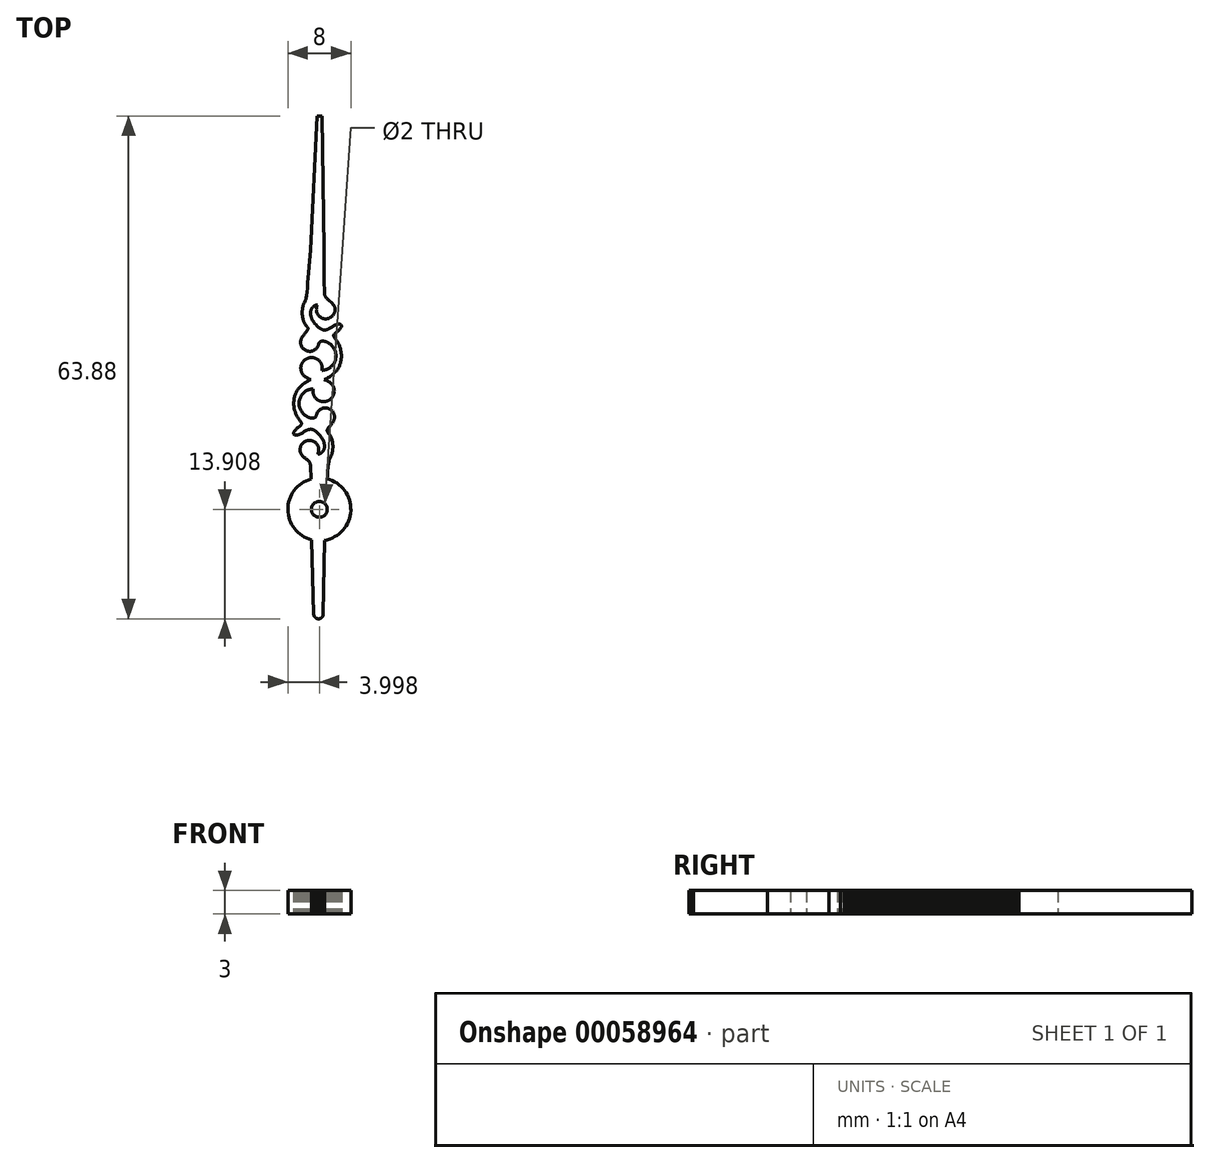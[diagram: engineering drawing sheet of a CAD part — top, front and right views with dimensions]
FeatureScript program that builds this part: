
annotation { "Feature Type Name" : "Feature", "Feature Type Description" : "" }
export const myFeature = defineFeature(function(context is Context, id is Id, definition is map)
    precondition{}
    {
        {
            var Q0;
            Q0=qCreatedBy(makeId("Top.planeOp"),FACE);
            var sketch = newSketch(context, id + "F0", { "sketchPlane" : qUnion([Q0])});
            skLineSegment(sketch, "E0", {"start": v(-0.08, 31.94) * mm, "end": v(0.58, 31.94) * mm});
            skLineSegment(sketch, "E1", {"start": v(0.58, 31.94) * mm, "end": v(0.8, 15.02) * mm});
            skLineSegment(sketch, "E2", {"start": v(0.8, 15.02) * mm, "end": v(0.8, 13.68) * mm});
            skLineSegment(sketch, "E3", {"start": v(0.8, 13.68) * mm, "end": v(0.82, 12.32) * mm});
            skLineSegment(sketch, "E4", {"start": v(0.82, 12.32) * mm, "end": v(0.83, 11.67) * mm});
            skLineSegment(sketch, "E5", {"start": v(0.83, 11.67) * mm, "end": v(0.84, 11.05) * mm});
            skLineSegment(sketch, "E6", {"start": v(0.84, 11.05) * mm, "end": v(0.85, 10.49) * mm});
            skLineSegment(sketch, "E7", {"start": v(0.85, 10.49) * mm, "end": v(0.87, 10) * mm});
            skLineSegment(sketch, "E8", {"start": v(0.87, 10) * mm, "end": v(0.89, 9.58) * mm});
            skLineSegment(sketch, "E9", {"start": v(0.89, 9.58) * mm, "end": v(0.9, 9.27) * mm});
            skLineSegment(sketch, "E10", {"start": v(0.9, 9.27) * mm, "end": v(0.92, 9.18) * mm});
            skLineSegment(sketch, "E11", {"start": v(0.92, 9.18) * mm, "end": v(0.94, 9.1) * mm});
            skLineSegment(sketch, "E12", {"start": v(0.94, 9.1) * mm, "end": v(0.97, 9.03) * mm});
            skLineSegment(sketch, "E13", {"start": v(0.97, 9.03) * mm, "end": v(1, 8.97) * mm});
            skLineSegment(sketch, "E14", {"start": v(1, 8.97) * mm, "end": v(1.03, 8.9) * mm});
            skLineSegment(sketch, "E15", {"start": v(1.03, 8.9) * mm, "end": v(1.07, 8.85) * mm});
            skLineSegment(sketch, "E16", {"start": v(1.07, 8.85) * mm, "end": v(1.12, 8.8) * mm});
            skLineSegment(sketch, "E17", {"start": v(1.12, 8.8) * mm, "end": v(1.16, 8.76) * mm});
            skLineSegment(sketch, "E18", {"start": v(1.16, 8.76) * mm, "end": v(1.26, 8.67) * mm});
            skLineSegment(sketch, "E19", {"start": v(1.26, 8.67) * mm, "end": v(1.36, 8.59) * mm});
            skLineSegment(sketch, "E20", {"start": v(1.36, 8.59) * mm, "end": v(1.45, 8.5) * mm});
            skLineSegment(sketch, "E21", {"start": v(1.45, 8.5) * mm, "end": v(1.5, 8.46) * mm});
            skLineSegment(sketch, "E22", {"start": v(1.5, 8.46) * mm, "end": v(1.54, 8.42) * mm});
            skLineSegment(sketch, "E23", {"start": v(1.54, 8.42) * mm, "end": v(1.54, 8.42) * mm});
            skLineSegment(sketch, "E24", {"start": v(1.54, 8.42) * mm, "end": v(1.69, 8.3) * mm});
            skLineSegment(sketch, "E25", {"start": v(1.69, 8.3) * mm, "end": v(1.76, 8.25) * mm});
            skLineSegment(sketch, "E26", {"start": v(1.76, 8.25) * mm, "end": v(1.82, 8.19) * mm});
            skLineSegment(sketch, "E27", {"start": v(1.82, 8.19) * mm, "end": v(1.88, 8.13) * mm});
            skLineSegment(sketch, "E28", {"start": v(1.88, 8.13) * mm, "end": v(1.94, 8.07) * mm});
            skLineSegment(sketch, "E29", {"start": v(1.94, 8.07) * mm, "end": v(2, 8) * mm});
            skLineSegment(sketch, "E30", {"start": v(2, 8) * mm, "end": v(2.04, 7.94) * mm});
            skLineSegment(sketch, "E31", {"start": v(2.04, 7.94) * mm, "end": v(2.08, 7.88) * mm});
            skLineSegment(sketch, "E32", {"start": v(2.08, 7.88) * mm, "end": v(2.12, 7.81) * mm});
            skLineSegment(sketch, "E33", {"start": v(2.12, 7.81) * mm, "end": v(2.15, 7.74) * mm});
            skLineSegment(sketch, "E34", {"start": v(2.15, 7.74) * mm, "end": v(2.17, 7.67) * mm});
            skLineSegment(sketch, "E35", {"start": v(2.17, 7.67) * mm, "end": v(2.2, 7.6) * mm});
            skLineSegment(sketch, "E36", {"start": v(2.2, 7.6) * mm, "end": v(2.2, 7.52) * mm});
            skLineSegment(sketch, "E37", {"start": v(2.2, 7.52) * mm, "end": v(2.22, 7.43) * mm});
            skLineSegment(sketch, "E38", {"start": v(2.22, 7.43) * mm, "end": v(2.22, 7.35) * mm});
            skLineSegment(sketch, "E39", {"start": v(2.22, 7.35) * mm, "end": v(2.22, 7.28) * mm});
            skLineSegment(sketch, "E40", {"start": v(2.22, 7.28) * mm, "end": v(2.21, 7.22) * mm});
            skLineSegment(sketch, "E41", {"start": v(2.21, 7.22) * mm, "end": v(2.2, 7.16) * mm});
            skLineSegment(sketch, "E42", {"start": v(2.2, 7.16) * mm, "end": v(2.2, 7.1) * mm});
            skLineSegment(sketch, "E43", {"start": v(2.2, 7.1) * mm, "end": v(2.18, 7.05) * mm});
            skLineSegment(sketch, "E44", {"start": v(2.18, 7.05) * mm, "end": v(2.17, 7) * mm});
            skLineSegment(sketch, "E45", {"start": v(2.17, 7) * mm, "end": v(2.15, 6.94) * mm});
            skLineSegment(sketch, "E46", {"start": v(2.15, 6.94) * mm, "end": v(2.13, 6.88) * mm});
            skLineSegment(sketch, "E47", {"start": v(2.13, 6.88) * mm, "end": v(2.1, 6.83) * mm});
            skLineSegment(sketch, "E48", {"start": v(2.1, 6.83) * mm, "end": v(2.08, 6.78) * mm});
            skLineSegment(sketch, "E49", {"start": v(2.08, 6.78) * mm, "end": v(2.02, 6.68) * mm});
            skLineSegment(sketch, "E50", {"start": v(2.02, 6.68) * mm, "end": v(1.95, 6.59) * mm});
            skLineSegment(sketch, "E51", {"start": v(1.95, 6.59) * mm, "end": v(1.87, 6.5) * mm});
            skLineSegment(sketch, "E52", {"start": v(1.87, 6.5) * mm, "end": v(1.79, 6.43) * mm});
            skLineSegment(sketch, "E53", {"start": v(1.79, 6.43) * mm, "end": v(1.7, 6.36) * mm});
            skLineSegment(sketch, "E54", {"start": v(1.7, 6.36) * mm, "end": v(1.6, 6.3) * mm});
            skLineSegment(sketch, "E55", {"start": v(1.6, 6.3) * mm, "end": v(1.55, 6.27) * mm});
            skLineSegment(sketch, "E56", {"start": v(1.55, 6.27) * mm, "end": v(1.5, 6.25) * mm});
            skLineSegment(sketch, "E57", {"start": v(1.5, 6.25) * mm, "end": v(1.44, 6.23) * mm});
            skLineSegment(sketch, "E58", {"start": v(1.44, 6.23) * mm, "end": v(1.39, 6.21) * mm});
            skLineSegment(sketch, "E59", {"start": v(1.39, 6.21) * mm, "end": v(1.33, 6.2) * mm});
            skLineSegment(sketch, "E60", {"start": v(1.33, 6.2) * mm, "end": v(1.27, 6.18) * mm});
            skLineSegment(sketch, "E61", {"start": v(1.27, 6.18) * mm, "end": v(1.21, 6.17) * mm});
            skLineSegment(sketch, "E62", {"start": v(1.21, 6.17) * mm, "end": v(1.15, 6.16) * mm});
            skLineSegment(sketch, "E63", {"start": v(1.15, 6.16) * mm, "end": v(1.1, 6.16) * mm});
            skLineSegment(sketch, "E64", {"start": v(1.1, 6.16) * mm, "end": v(1.03, 6.16) * mm});
            skLineSegment(sketch, "E65", {"start": v(1.03, 6.16) * mm, "end": v(0.97, 6.16) * mm});
            skLineSegment(sketch, "E66", {"start": v(0.97, 6.16) * mm, "end": v(0.91, 6.16) * mm});
            skLineSegment(sketch, "E67", {"start": v(0.91, 6.16) * mm, "end": v(0.85, 6.17) * mm});
            skLineSegment(sketch, "E68", {"start": v(0.85, 6.17) * mm, "end": v(0.8, 6.18) * mm});
            skLineSegment(sketch, "E69", {"start": v(0.8, 6.18) * mm, "end": v(0.74, 6.2) * mm});
            skLineSegment(sketch, "E70", {"start": v(0.74, 6.2) * mm, "end": v(0.68, 6.21) * mm});
            skLineSegment(sketch, "E71", {"start": v(0.68, 6.21) * mm, "end": v(0.62, 6.23) * mm});
            skLineSegment(sketch, "E72", {"start": v(0.62, 6.23) * mm, "end": v(0.57, 6.25) * mm});
            skLineSegment(sketch, "E73", {"start": v(0.57, 6.25) * mm, "end": v(0.52, 6.27) * mm});
            skLineSegment(sketch, "E74", {"start": v(0.52, 6.27) * mm, "end": v(0.47, 6.3) * mm});
            skLineSegment(sketch, "E75", {"start": v(0.47, 6.3) * mm, "end": v(0.37, 6.36) * mm});
            skLineSegment(sketch, "E76", {"start": v(0.37, 6.36) * mm, "end": v(0.28, 6.43) * mm});
            skLineSegment(sketch, "E77", {"start": v(0.28, 6.43) * mm, "end": v(0.2, 6.5) * mm});
            skLineSegment(sketch, "E78", {"start": v(0.2, 6.5) * mm, "end": v(0.12, 6.59) * mm});
            skLineSegment(sketch, "E79", {"start": v(0.12, 6.59) * mm, "end": v(0.05, 6.68) * mm});
            skLineSegment(sketch, "E80", {"start": v(0.05, 6.68) * mm, "end": v(-0.01, 6.78) * mm});
            skLineSegment(sketch, "E81", {"start": v(-0.01, 6.78) * mm, "end": v(-0.04, 6.83) * mm});
            skLineSegment(sketch, "E82", {"start": v(-0.04, 6.83) * mm, "end": v(-0.06, 6.88) * mm});
            skLineSegment(sketch, "E83", {"start": v(-0.06, 6.88) * mm, "end": v(-0.08, 6.94) * mm});
            skLineSegment(sketch, "E84", {"start": v(-0.08, 6.94) * mm, "end": v(-0.1, 7) * mm});
            skLineSegment(sketch, "E85", {"start": v(-0.1, 7) * mm, "end": v(-0.12, 7.05) * mm});
            skLineSegment(sketch, "E86", {"start": v(-0.12, 7.05) * mm, "end": v(-0.13, 7.1) * mm});
            skLineSegment(sketch, "E87", {"start": v(-0.13, 7.1) * mm, "end": v(-0.14, 7.16) * mm});
            skLineSegment(sketch, "E88", {"start": v(-0.14, 7.16) * mm, "end": v(-0.15, 7.22) * mm});
            skLineSegment(sketch, "E89", {"start": v(-0.15, 7.22) * mm, "end": v(-0.15, 7.28) * mm});
            skLineSegment(sketch, "E90", {"start": v(-0.15, 7.28) * mm, "end": v(-0.16, 7.35) * mm});
            skLineSegment(sketch, "E91", {"start": v(-0.16, 7.35) * mm, "end": v(-0.15, 7.42) * mm});
            skLineSegment(sketch, "E92", {"start": v(-0.15, 7.42) * mm, "end": v(-0.15, 7.5) * mm});
            skLineSegment(sketch, "E93", {"start": v(-0.15, 7.5) * mm, "end": v(-0.13, 7.58) * mm});
            skLineSegment(sketch, "E94", {"start": v(-0.13, 7.58) * mm, "end": v(-0.12, 7.65) * mm});
            skLineSegment(sketch, "E95", {"start": v(-0.12, 7.65) * mm, "end": v(-0.1, 7.73) * mm});
            skLineSegment(sketch, "E96", {"start": v(-0.1, 7.73) * mm, "end": v(-0.07, 7.8) * mm});
            skLineSegment(sketch, "E97", {"start": v(-0.07, 7.8) * mm, "end": v(-0.04, 7.87) * mm});
            skLineSegment(sketch, "E98", {"start": v(-0.04, 7.87) * mm, "end": v(0, 7.93) * mm});
            skLineSegment(sketch, "E99", {"start": v(0, 7.93) * mm, "end": v(-0.03, 7.93) * mm});
            skLineSegment(sketch, "E100", {"start": v(-0.03, 7.93) * mm, "end": v(-0.07, 7.92) * mm});
            skLineSegment(sketch, "E101", {"start": v(-0.07, 7.92) * mm, "end": v(-0.17, 7.88) * mm});
            skLineSegment(sketch, "E102", {"start": v(-0.17, 7.88) * mm, "end": v(-0.3, 7.83) * mm});
            skLineSegment(sketch, "E103", {"start": v(-0.3, 7.83) * mm, "end": v(-0.44, 7.76) * mm});
            skLineSegment(sketch, "E104", {"start": v(-0.44, 7.76) * mm, "end": v(-0.5, 7.72) * mm});
            skLineSegment(sketch, "E105", {"start": v(-0.5, 7.72) * mm, "end": v(-0.55, 7.69) * mm});
            skLineSegment(sketch, "E106", {"start": v(-0.55, 7.69) * mm, "end": v(-0.6, 7.65) * mm});
            skLineSegment(sketch, "E107", {"start": v(-0.6, 7.65) * mm, "end": v(-0.65, 7.6) * mm});
            skLineSegment(sketch, "E108", {"start": v(-0.65, 7.6) * mm, "end": v(-0.69, 7.56) * mm});
            skLineSegment(sketch, "E109", {"start": v(-0.69, 7.56) * mm, "end": v(-0.72, 7.5) * mm});
            skLineSegment(sketch, "E110", {"start": v(-0.72, 7.5) * mm, "end": v(-0.76, 7.45) * mm});
            skLineSegment(sketch, "E111", {"start": v(-0.76, 7.45) * mm, "end": v(-0.79, 7.4) * mm});
            skLineSegment(sketch, "E112", {"start": v(-0.79, 7.4) * mm, "end": v(-0.81, 7.34) * mm});
            skLineSegment(sketch, "E113", {"start": v(-0.81, 7.34) * mm, "end": v(-0.84, 7.27) * mm});
            skLineSegment(sketch, "E114", {"start": v(-0.84, 7.27) * mm, "end": v(-0.85, 7.2) * mm});
            skLineSegment(sketch, "E115", {"start": v(-0.85, 7.2) * mm, "end": v(-0.87, 7.14) * mm});
            skLineSegment(sketch, "E116", {"start": v(-0.87, 7.14) * mm, "end": v(-0.88, 7.07) * mm});
            skLineSegment(sketch, "E117", {"start": v(-0.88, 7.07) * mm, "end": v(-0.88, 7) * mm});
            skLineSegment(sketch, "E118", {"start": v(-0.88, 7) * mm, "end": v(-0.89, 6.93) * mm});
            skLineSegment(sketch, "E119", {"start": v(-0.89, 6.93) * mm, "end": v(-0.89, 6.86) * mm});
            skLineSegment(sketch, "E120", {"start": v(-0.89, 6.86) * mm, "end": v(-0.88, 6.78) * mm});
            skLineSegment(sketch, "E121", {"start": v(-0.88, 6.78) * mm, "end": v(-0.87, 6.7) * mm});
            skLineSegment(sketch, "E122", {"start": v(-0.87, 6.7) * mm, "end": v(-0.86, 6.62) * mm});
            skLineSegment(sketch, "E123", {"start": v(-0.86, 6.62) * mm, "end": v(-0.84, 6.55) * mm});
            skLineSegment(sketch, "E124", {"start": v(-0.84, 6.55) * mm, "end": v(-0.82, 6.46) * mm});
            skLineSegment(sketch, "E125", {"start": v(-0.82, 6.46) * mm, "end": v(-0.8, 6.38) * mm});
            skLineSegment(sketch, "E126", {"start": v(-0.8, 6.38) * mm, "end": v(-0.77, 6.3) * mm});
            skLineSegment(sketch, "E127", {"start": v(-0.77, 6.3) * mm, "end": v(-0.74, 6.22) * mm});
            skLineSegment(sketch, "E128", {"start": v(-0.74, 6.22) * mm, "end": v(-0.7, 6.14) * mm});
            skLineSegment(sketch, "E129", {"start": v(-0.7, 6.14) * mm, "end": v(-0.67, 6.06) * mm});
            skLineSegment(sketch, "E130", {"start": v(-0.67, 6.06) * mm, "end": v(-0.62, 5.98) * mm});
            skLineSegment(sketch, "E131", {"start": v(-0.62, 5.98) * mm, "end": v(-0.58, 5.9) * mm});
            skLineSegment(sketch, "E132", {"start": v(-0.58, 5.9) * mm, "end": v(-0.53, 5.82) * mm});
            skLineSegment(sketch, "E133", {"start": v(-0.53, 5.82) * mm, "end": v(-0.47, 5.74) * mm});
            skLineSegment(sketch, "E134", {"start": v(-0.47, 5.74) * mm, "end": v(-0.42, 5.66) * mm});
            skLineSegment(sketch, "E135", {"start": v(-0.42, 5.66) * mm, "end": v(-0.35, 5.58) * mm});
            skLineSegment(sketch, "E136", {"start": v(-0.35, 5.58) * mm, "end": v(-0.22, 5.41) * mm});
            skLineSegment(sketch, "E137", {"start": v(-0.22, 5.41) * mm, "end": v(-0.08, 5.27) * mm});
            skLineSegment(sketch, "E138", {"start": v(-0.08, 5.27) * mm, "end": v(0.05, 5.14) * mm});
            skLineSegment(sketch, "E139", {"start": v(0.05, 5.14) * mm, "end": v(0.11, 5.08) * mm});
            skLineSegment(sketch, "E140", {"start": v(0.11, 5.08) * mm, "end": v(0.18, 5.03) * mm});
            skLineSegment(sketch, "E141", {"start": v(0.18, 5.03) * mm, "end": v(0.24, 4.98) * mm});
            skLineSegment(sketch, "E142", {"start": v(0.24, 4.98) * mm, "end": v(0.3, 4.94) * mm});
            skLineSegment(sketch, "E143", {"start": v(0.3, 4.94) * mm, "end": v(0.36, 4.9) * mm});
            skLineSegment(sketch, "E144", {"start": v(0.36, 4.9) * mm, "end": v(0.42, 4.87) * mm});
            skLineSegment(sketch, "E145", {"start": v(0.42, 4.87) * mm, "end": v(0.48, 4.84) * mm});
            skLineSegment(sketch, "E146", {"start": v(0.48, 4.84) * mm, "end": v(0.54, 4.81) * mm});
            skLineSegment(sketch, "E147", {"start": v(0.54, 4.81) * mm, "end": v(0.6, 4.79) * mm});
            skLineSegment(sketch, "E148", {"start": v(0.6, 4.79) * mm, "end": v(0.66, 4.77) * mm});
            skLineSegment(sketch, "E149", {"start": v(0.66, 4.77) * mm, "end": v(0.72, 4.76) * mm});
            skLineSegment(sketch, "E150", {"start": v(0.72, 4.76) * mm, "end": v(0.78, 4.75) * mm});
            skLineSegment(sketch, "E151", {"start": v(0.78, 4.75) * mm, "end": v(0.85, 4.75) * mm});
            skLineSegment(sketch, "E152", {"start": v(0.85, 4.75) * mm, "end": v(0.9, 4.74) * mm});
            skLineSegment(sketch, "E153", {"start": v(0.9, 4.74) * mm, "end": v(0.97, 4.75) * mm});
            skLineSegment(sketch, "E154", {"start": v(0.97, 4.75) * mm, "end": v(1.03, 4.76) * mm});
            skLineSegment(sketch, "E155", {"start": v(1.03, 4.76) * mm, "end": v(1.1, 4.77) * mm});
            skLineSegment(sketch, "E156", {"start": v(1.1, 4.77) * mm, "end": v(1.16, 4.79) * mm});
            skLineSegment(sketch, "E157", {"start": v(1.16, 4.79) * mm, "end": v(1.22, 4.8) * mm});
            skLineSegment(sketch, "E158", {"start": v(1.22, 4.8) * mm, "end": v(1.29, 4.83) * mm});
            skLineSegment(sketch, "E159", {"start": v(1.29, 4.83) * mm, "end": v(1.35, 4.86) * mm});
            skLineSegment(sketch, "E160", {"start": v(1.35, 4.86) * mm, "end": v(1.42, 4.9) * mm});
            skLineSegment(sketch, "E161", {"start": v(1.42, 4.9) * mm, "end": v(1.49, 4.93) * mm});
            skLineSegment(sketch, "E162", {"start": v(1.49, 4.93) * mm, "end": v(1.56, 4.97) * mm});
            skLineSegment(sketch, "E163", {"start": v(1.56, 4.97) * mm, "end": v(1.7, 5.06) * mm});
            skLineSegment(sketch, "E164", {"start": v(1.7, 5.06) * mm, "end": v(1.81, 5.14) * mm});
            skLineSegment(sketch, "E165", {"start": v(1.81, 5.14) * mm, "end": v(1.92, 5.2) * mm});
            skLineSegment(sketch, "E166", {"start": v(1.92, 5.2) * mm, "end": v(2.03, 5.26) * mm});
            skLineSegment(sketch, "E167", {"start": v(2.03, 5.26) * mm, "end": v(2.13, 5.31) * mm});
            skLineSegment(sketch, "E168", {"start": v(2.13, 5.31) * mm, "end": v(2.22, 5.36) * mm});
            skLineSegment(sketch, "E169", {"start": v(2.22, 5.36) * mm, "end": v(2.32, 5.4) * mm});
            skLineSegment(sketch, "E170", {"start": v(2.32, 5.4) * mm, "end": v(2.4, 5.43) * mm});
            skLineSegment(sketch, "E171", {"start": v(2.4, 5.43) * mm, "end": v(2.49, 5.45) * mm});
            skLineSegment(sketch, "E172", {"start": v(2.49, 5.45) * mm, "end": v(2.57, 5.47) * mm});
            skLineSegment(sketch, "E173", {"start": v(2.57, 5.47) * mm, "end": v(2.64, 5.48) * mm});
            skLineSegment(sketch, "E174", {"start": v(2.64, 5.48) * mm, "end": v(2.71, 5.49) * mm});
            skLineSegment(sketch, "E175", {"start": v(2.71, 5.49) * mm, "end": v(2.77, 5.49) * mm});
            skLineSegment(sketch, "E176", {"start": v(2.77, 5.49) * mm, "end": v(2.83, 5.48) * mm});
            skLineSegment(sketch, "E177", {"start": v(2.83, 5.48) * mm, "end": v(2.88, 5.47) * mm});
            skLineSegment(sketch, "E178", {"start": v(2.88, 5.47) * mm, "end": v(2.93, 5.45) * mm});
            skLineSegment(sketch, "E179", {"start": v(2.93, 5.45) * mm, "end": v(2.96, 5.43) * mm});
            skLineSegment(sketch, "E180", {"start": v(2.96, 5.43) * mm, "end": v(3, 5.4) * mm});
            skLineSegment(sketch, "E181", {"start": v(3, 5.4) * mm, "end": v(3.02, 5.37) * mm});
            skLineSegment(sketch, "E182", {"start": v(3.02, 5.37) * mm, "end": v(3.04, 5.34) * mm});
            skLineSegment(sketch, "E183", {"start": v(3.04, 5.34) * mm, "end": v(3.05, 5.3) * mm});
            skLineSegment(sketch, "E184", {"start": v(3.05, 5.3) * mm, "end": v(3.05, 5.25) * mm});
            skLineSegment(sketch, "E185", {"start": v(3.05, 5.25) * mm, "end": v(3.04, 5.2) * mm});
            skLineSegment(sketch, "E186", {"start": v(3.04, 5.2) * mm, "end": v(3.03, 5.15) * mm});
            skLineSegment(sketch, "E187", {"start": v(3.03, 5.15) * mm, "end": v(3, 5.1) * mm});
            skLineSegment(sketch, "E188", {"start": v(3, 5.1) * mm, "end": v(2.97, 5.03) * mm});
            skLineSegment(sketch, "E189", {"start": v(2.97, 5.03) * mm, "end": v(2.93, 4.97) * mm});
            skLineSegment(sketch, "E190", {"start": v(2.93, 4.97) * mm, "end": v(2.88, 4.9) * mm});
            skLineSegment(sketch, "E191", {"start": v(2.88, 4.9) * mm, "end": v(2.82, 4.83) * mm});
            skLineSegment(sketch, "E192", {"start": v(2.82, 4.83) * mm, "end": v(2.75, 4.76) * mm});
            skLineSegment(sketch, "E193", {"start": v(2.75, 4.76) * mm, "end": v(2.67, 4.68) * mm});
            skLineSegment(sketch, "E194", {"start": v(2.67, 4.68) * mm, "end": v(2.58, 4.6) * mm});
            skLineSegment(sketch, "E195", {"start": v(2.58, 4.6) * mm, "end": v(2.48, 4.52) * mm});
            skLineSegment(sketch, "E196", {"start": v(2.48, 4.52) * mm, "end": v(2.3, 4.38) * mm});
            skLineSegment(sketch, "E197", {"start": v(2.3, 4.38) * mm, "end": v(2.22, 4.31) * mm});
            skLineSegment(sketch, "E198", {"start": v(2.22, 4.31) * mm, "end": v(2.16, 4.26) * mm});
            skLineSegment(sketch, "E199", {"start": v(2.16, 4.26) * mm, "end": v(2.11, 4.2) * mm});
            skLineSegment(sketch, "E200", {"start": v(2.11, 4.2) * mm, "end": v(2.08, 4.15) * mm});
            skLineSegment(sketch, "E201", {"start": v(2.08, 4.15) * mm, "end": v(2.06, 4.12) * mm});
            skLineSegment(sketch, "E202", {"start": v(2.06, 4.12) * mm, "end": v(2.06, 4.1) * mm});
            skLineSegment(sketch, "E203", {"start": v(2.06, 4.1) * mm, "end": v(2.05, 4.07) * mm});
            skLineSegment(sketch, "E204", {"start": v(2.05, 4.07) * mm, "end": v(2.05, 4.04) * mm});
            skLineSegment(sketch, "E205", {"start": v(2.05, 4.04) * mm, "end": v(2.05, 4.01) * mm});
            skLineSegment(sketch, "E206", {"start": v(2.05, 4.01) * mm, "end": v(2.05, 3.98) * mm});
            skLineSegment(sketch, "E207", {"start": v(2.05, 3.98) * mm, "end": v(2.07, 3.92) * mm});
            skLineSegment(sketch, "E208", {"start": v(2.07, 3.92) * mm, "end": v(2.1, 3.85) * mm});
            skLineSegment(sketch, "E209", {"start": v(2.1, 3.85) * mm, "end": v(2.15, 3.76) * mm});
            skLineSegment(sketch, "E210", {"start": v(2.15, 3.76) * mm, "end": v(2.2, 3.67) * mm});
            skLineSegment(sketch, "E211", {"start": v(2.2, 3.67) * mm, "end": v(2.28, 3.57) * mm});
            skLineSegment(sketch, "E212", {"start": v(2.28, 3.57) * mm, "end": v(2.46, 3.31) * mm});
            skLineSegment(sketch, "E213", {"start": v(2.46, 3.31) * mm, "end": v(2.53, 3.2) * mm});
            skLineSegment(sketch, "E214", {"start": v(2.53, 3.2) * mm, "end": v(2.6, 3.1) * mm});
            skLineSegment(sketch, "E215", {"start": v(2.6, 3.1) * mm, "end": v(2.66, 3) * mm});
            skLineSegment(sketch, "E216", {"start": v(2.66, 3) * mm, "end": v(2.71, 2.88) * mm});
            skLineSegment(sketch, "E217", {"start": v(2.71, 2.88) * mm, "end": v(2.77, 2.76) * mm});
            skLineSegment(sketch, "E218", {"start": v(2.77, 2.76) * mm, "end": v(2.81, 2.64) * mm});
            skLineSegment(sketch, "E219", {"start": v(2.81, 2.64) * mm, "end": v(2.86, 2.52) * mm});
            skLineSegment(sketch, "E220", {"start": v(2.86, 2.52) * mm, "end": v(2.9, 2.4) * mm});
            skLineSegment(sketch, "E221", {"start": v(2.9, 2.4) * mm, "end": v(2.93, 2.27) * mm});
            skLineSegment(sketch, "E222", {"start": v(2.93, 2.27) * mm, "end": v(2.96, 2.15) * mm});
            skLineSegment(sketch, "E223", {"start": v(2.96, 2.15) * mm, "end": v(2.98, 2.02) * mm});
            skLineSegment(sketch, "E224", {"start": v(2.98, 2.02) * mm, "end": v(3, 1.9) * mm});
            skLineSegment(sketch, "E225", {"start": v(3, 1.9) * mm, "end": v(3.01, 1.77) * mm});
            skLineSegment(sketch, "E226", {"start": v(3.01, 1.77) * mm, "end": v(3.02, 1.64) * mm});
            skLineSegment(sketch, "E227", {"start": v(3.02, 1.64) * mm, "end": v(3.03, 1.51) * mm});
            skLineSegment(sketch, "E228", {"start": v(3.03, 1.51) * mm, "end": v(3.03, 1.38) * mm});
            skLineSegment(sketch, "E229", {"start": v(3.03, 1.38) * mm, "end": v(3.02, 1.26) * mm});
            skLineSegment(sketch, "E230", {"start": v(3.02, 1.26) * mm, "end": v(3.01, 1.13) * mm});
            skLineSegment(sketch, "E231", {"start": v(3.01, 1.13) * mm, "end": v(3, 1) * mm});
            skLineSegment(sketch, "E232", {"start": v(3, 1) * mm, "end": v(2.98, 0.88) * mm});
            skLineSegment(sketch, "E233", {"start": v(2.98, 0.88) * mm, "end": v(2.95, 0.75) * mm});
            skLineSegment(sketch, "E234", {"start": v(2.95, 0.75) * mm, "end": v(2.93, 0.63) * mm});
            skLineSegment(sketch, "E235", {"start": v(2.93, 0.63) * mm, "end": v(2.9, 0.51) * mm});
            skLineSegment(sketch, "E236", {"start": v(2.9, 0.51) * mm, "end": v(2.86, 0.4) * mm});
            skLineSegment(sketch, "E237", {"start": v(2.86, 0.4) * mm, "end": v(2.81, 0.28) * mm});
            skLineSegment(sketch, "E238", {"start": v(2.81, 0.28) * mm, "end": v(2.77, 0.17) * mm});
            skLineSegment(sketch, "E239", {"start": v(2.77, 0.17) * mm, "end": v(2.71, 0.06) * mm});
            skLineSegment(sketch, "E240", {"start": v(2.71, 0.06) * mm, "end": v(2.66, -0.05) * mm});
            skLineSegment(sketch, "E241", {"start": v(2.66, -0.05) * mm, "end": v(2.6, -0.15) * mm});
            skLineSegment(sketch, "E242", {"start": v(2.6, -0.15) * mm, "end": v(2.53, -0.25) * mm});
            skLineSegment(sketch, "E243", {"start": v(2.53, -0.25) * mm, "end": v(2.46, -0.35) * mm});
            skLineSegment(sketch, "E244", {"start": v(2.46, -0.35) * mm, "end": v(2.39, -0.44) * mm});
            skLineSegment(sketch, "E245", {"start": v(2.39, -0.44) * mm, "end": v(2.25, -0.59) * mm});
            skLineSegment(sketch, "E246", {"start": v(2.25, -0.59) * mm, "end": v(2.1, -0.73) * mm});
            skLineSegment(sketch, "E247", {"start": v(2.1, -0.73) * mm, "end": v(1.96, -0.87) * mm});
            skLineSegment(sketch, "E248", {"start": v(1.96, -0.87) * mm, "end": v(1.81, -1) * mm});
            skLineSegment(sketch, "E249", {"start": v(1.81, -1) * mm, "end": v(1.66, -1.1) * mm});
            skLineSegment(sketch, "E250", {"start": v(1.66, -1.1) * mm, "end": v(1.5, -1.22) * mm});
            skLineSegment(sketch, "E251", {"start": v(1.5, -1.22) * mm, "end": v(1.35, -1.31) * mm});
            skLineSegment(sketch, "E252", {"start": v(1.35, -1.31) * mm, "end": v(1.2, -1.4) * mm});
            skLineSegment(sketch, "E253", {"start": v(1.2, -1.4) * mm, "end": v(1.03, -1.48) * mm});
            skLineSegment(sketch, "E254", {"start": v(1.03, -1.48) * mm, "end": v(0.87, -1.55) * mm});
            skLineSegment(sketch, "E255", {"start": v(0.87, -1.55) * mm, "end": v(0.85, -1.55) * mm});
            skLineSegment(sketch, "E256", {"start": v(0.85, -1.55) * mm, "end": v(0.94, -1.59) * mm});
            skLineSegment(sketch, "E257", {"start": v(0.94, -1.59) * mm, "end": v(1.06, -1.64) * mm});
            skLineSegment(sketch, "E258", {"start": v(1.06, -1.64) * mm, "end": v(1.26, -1.73) * mm});
            skLineSegment(sketch, "E259", {"start": v(1.26, -1.73) * mm, "end": v(1.4, -1.8) * mm});
            skLineSegment(sketch, "E260", {"start": v(1.4, -1.8) * mm, "end": v(1.47, -1.83) * mm});
            skLineSegment(sketch, "E261", {"start": v(1.47, -1.83) * mm, "end": v(1.54, -1.88) * mm});
            skLineSegment(sketch, "E262", {"start": v(1.54, -1.88) * mm, "end": v(1.6, -1.93) * mm});
            skLineSegment(sketch, "E263", {"start": v(1.6, -1.93) * mm, "end": v(1.67, -1.99) * mm});
            skLineSegment(sketch, "E264", {"start": v(1.67, -1.99) * mm, "end": v(1.74, -2.05) * mm});
            skLineSegment(sketch, "E265", {"start": v(1.74, -2.05) * mm, "end": v(1.8, -2.1) * mm});
            skLineSegment(sketch, "E266", {"start": v(1.8, -2.1) * mm, "end": v(1.85, -2.18) * mm});
            skLineSegment(sketch, "E267", {"start": v(1.85, -2.18) * mm, "end": v(1.9, -2.25) * mm});
            skLineSegment(sketch, "E268", {"start": v(1.9, -2.25) * mm, "end": v(1.95, -2.32) * mm});
            skLineSegment(sketch, "E269", {"start": v(1.95, -2.32) * mm, "end": v(1.99, -2.4) * mm});
            skLineSegment(sketch, "E270", {"start": v(1.99, -2.4) * mm, "end": v(2.02, -2.48) * mm});
            skLineSegment(sketch, "E271", {"start": v(2.02, -2.48) * mm, "end": v(2.06, -2.56) * mm});
            skLineSegment(sketch, "E272", {"start": v(2.06, -2.56) * mm, "end": v(2.08, -2.64) * mm});
            skLineSegment(sketch, "E273", {"start": v(2.08, -2.64) * mm, "end": v(2.1, -2.73) * mm});
            skLineSegment(sketch, "E274", {"start": v(2.1, -2.73) * mm, "end": v(2.12, -2.82) * mm});
            skLineSegment(sketch, "E275", {"start": v(2.12, -2.82) * mm, "end": v(2.13, -2.9) * mm});
            skLineSegment(sketch, "E276", {"start": v(2.13, -2.9) * mm, "end": v(2.13, -3) * mm});
            skLineSegment(sketch, "E277", {"start": v(2.13, -3) * mm, "end": v(2.13, -3.07) * mm});
            skLineSegment(sketch, "E278", {"start": v(2.13, -3.07) * mm, "end": v(2.12, -3.14) * mm});
            skLineSegment(sketch, "E279", {"start": v(2.12, -3.14) * mm, "end": v(2.11, -3.2) * mm});
            skLineSegment(sketch, "E280", {"start": v(2.11, -3.2) * mm, "end": v(2.1, -3.28) * mm});
            skLineSegment(sketch, "E281", {"start": v(2.1, -3.28) * mm, "end": v(2.09, -3.34) * mm});
            skLineSegment(sketch, "E282", {"start": v(2.09, -3.34) * mm, "end": v(2.07, -3.4) * mm});
            skLineSegment(sketch, "E283", {"start": v(2.07, -3.4) * mm, "end": v(2.05, -3.47) * mm});
            skLineSegment(sketch, "E284", {"start": v(2.05, -3.47) * mm, "end": v(2.02, -3.53) * mm});
            skLineSegment(sketch, "E285", {"start": v(2.02, -3.53) * mm, "end": v(2, -3.6) * mm});
            skLineSegment(sketch, "E286", {"start": v(2, -3.6) * mm, "end": v(1.96, -3.65) * mm});
            skLineSegment(sketch, "E287", {"start": v(1.96, -3.65) * mm, "end": v(1.93, -3.7) * mm});
            skLineSegment(sketch, "E288", {"start": v(1.93, -3.7) * mm, "end": v(1.9, -3.76) * mm});
            skLineSegment(sketch, "E289", {"start": v(1.9, -3.76) * mm, "end": v(1.86, -3.82) * mm});
            skLineSegment(sketch, "E290", {"start": v(1.86, -3.82) * mm, "end": v(1.82, -3.87) * mm});
            skLineSegment(sketch, "E291", {"start": v(1.82, -3.87) * mm, "end": v(1.77, -3.92) * mm});
            skLineSegment(sketch, "E292", {"start": v(1.77, -3.92) * mm, "end": v(1.73, -3.97) * mm});
            skLineSegment(sketch, "E293", {"start": v(1.73, -3.97) * mm, "end": v(1.68, -4.01) * mm});
            skLineSegment(sketch, "E294", {"start": v(1.68, -4.01) * mm, "end": v(1.63, -4.05) * mm});
            skLineSegment(sketch, "E295", {"start": v(1.63, -4.05) * mm, "end": v(1.58, -4.1) * mm});
            skLineSegment(sketch, "E296", {"start": v(1.58, -4.1) * mm, "end": v(1.53, -4.13) * mm});
            skLineSegment(sketch, "E297", {"start": v(1.53, -4.13) * mm, "end": v(1.47, -4.17) * mm});
            skLineSegment(sketch, "E298", {"start": v(1.47, -4.17) * mm, "end": v(1.42, -4.2) * mm});
            skLineSegment(sketch, "E299", {"start": v(1.42, -4.2) * mm, "end": v(1.36, -4.23) * mm});
            skLineSegment(sketch, "E300", {"start": v(1.36, -4.23) * mm, "end": v(1.3, -4.26) * mm});
            skLineSegment(sketch, "E301", {"start": v(1.3, -4.26) * mm, "end": v(1.23, -4.28) * mm});
            skLineSegment(sketch, "E302", {"start": v(1.23, -4.28) * mm, "end": v(1.17, -4.3) * mm});
            skLineSegment(sketch, "E303", {"start": v(1.17, -4.3) * mm, "end": v(1.1, -4.32) * mm});
            skLineSegment(sketch, "E304", {"start": v(1.1, -4.32) * mm, "end": v(1.04, -4.34) * mm});
            skLineSegment(sketch, "E305", {"start": v(1.04, -4.34) * mm, "end": v(0.97, -4.35) * mm});
            skLineSegment(sketch, "E306", {"start": v(0.97, -4.35) * mm, "end": v(0.9, -4.36) * mm});
            skLineSegment(sketch, "E307", {"start": v(0.9, -4.36) * mm, "end": v(0.84, -4.36) * mm});
            skLineSegment(sketch, "E308", {"start": v(0.84, -4.36) * mm, "end": v(0.76, -4.37) * mm});
            skLineSegment(sketch, "E309", {"start": v(0.76, -4.37) * mm, "end": v(0.7, -4.36) * mm});
            skLineSegment(sketch, "E310", {"start": v(0.7, -4.36) * mm, "end": v(0.63, -4.36) * mm});
            skLineSegment(sketch, "E311", {"start": v(0.63, -4.36) * mm, "end": v(0.56, -4.35) * mm});
            skLineSegment(sketch, "E312", {"start": v(0.56, -4.35) * mm, "end": v(0.5, -4.34) * mm});
            skLineSegment(sketch, "E313", {"start": v(0.5, -4.34) * mm, "end": v(0.42, -4.32) * mm});
            skLineSegment(sketch, "E314", {"start": v(0.42, -4.32) * mm, "end": v(0.36, -4.3) * mm});
            skLineSegment(sketch, "E315", {"start": v(0.36, -4.3) * mm, "end": v(0.3, -4.28) * mm});
            skLineSegment(sketch, "E316", {"start": v(0.3, -4.28) * mm, "end": v(0.23, -4.26) * mm});
            skLineSegment(sketch, "E317", {"start": v(0.23, -4.26) * mm, "end": v(0.17, -4.23) * mm});
            skLineSegment(sketch, "E318", {"start": v(0.17, -4.23) * mm, "end": v(0.11, -4.2) * mm});
            skLineSegment(sketch, "E319", {"start": v(0.11, -4.2) * mm, "end": v(0.06, -4.17) * mm});
            skLineSegment(sketch, "E320", {"start": v(0.06, -4.17) * mm, "end": v(0, -4.13) * mm});
            skLineSegment(sketch, "E321", {"start": v(0, -4.13) * mm, "end": v(-0.05, -4.1) * mm});
            skLineSegment(sketch, "E322", {"start": v(-0.05, -4.1) * mm, "end": v(-0.1, -4.05) * mm});
            skLineSegment(sketch, "E323", {"start": v(-0.1, -4.05) * mm, "end": v(-0.15, -4.01) * mm});
            skLineSegment(sketch, "E324", {"start": v(-0.15, -4.01) * mm, "end": v(-0.2, -3.97) * mm});
            skLineSegment(sketch, "E325", {"start": v(-0.2, -3.97) * mm, "end": v(-0.24, -3.92) * mm});
            skLineSegment(sketch, "E326", {"start": v(-0.24, -3.92) * mm, "end": v(-0.29, -3.87) * mm});
            skLineSegment(sketch, "E327", {"start": v(-0.29, -3.87) * mm, "end": v(-0.33, -3.82) * mm});
            skLineSegment(sketch, "E328", {"start": v(-0.33, -3.82) * mm, "end": v(-0.37, -3.76) * mm});
            skLineSegment(sketch, "E329", {"start": v(-0.37, -3.76) * mm, "end": v(-0.4, -3.7) * mm});
            skLineSegment(sketch, "E330", {"start": v(-0.4, -3.7) * mm, "end": v(-0.43, -3.65) * mm});
            skLineSegment(sketch, "E331", {"start": v(-0.43, -3.65) * mm, "end": v(-0.46, -3.6) * mm});
            skLineSegment(sketch, "E332", {"start": v(-0.46, -3.6) * mm, "end": v(-0.5, -3.53) * mm});
            skLineSegment(sketch, "E333", {"start": v(-0.5, -3.53) * mm, "end": v(-0.52, -3.47) * mm});
            skLineSegment(sketch, "E334", {"start": v(-0.52, -3.47) * mm, "end": v(-0.54, -3.4) * mm});
            skLineSegment(sketch, "E335", {"start": v(-0.54, -3.4) * mm, "end": v(-0.56, -3.34) * mm});
            skLineSegment(sketch, "E336", {"start": v(-0.56, -3.34) * mm, "end": v(-0.57, -3.28) * mm});
            skLineSegment(sketch, "E337", {"start": v(-0.57, -3.28) * mm, "end": v(-0.58, -3.2) * mm});
            skLineSegment(sketch, "E338", {"start": v(-0.58, -3.2) * mm, "end": v(-0.6, -3.14) * mm});
            skLineSegment(sketch, "E339", {"start": v(-0.6, -3.14) * mm, "end": v(-0.6, -3.07) * mm});
            skLineSegment(sketch, "E340", {"start": v(-0.6, -3.07) * mm, "end": v(-0.6, -3) * mm});
            skLineSegment(sketch, "E341", {"start": v(-0.6, -3) * mm, "end": v(-0.6, -2.93) * mm});
            skLineSegment(sketch, "E342", {"start": v(-0.6, -2.93) * mm, "end": v(-0.6, -2.87) * mm});
            skLineSegment(sketch, "E343", {"start": v(-0.6, -2.87) * mm, "end": v(-0.58, -2.8) * mm});
            skLineSegment(sketch, "E344", {"start": v(-0.58, -2.8) * mm, "end": v(-0.57, -2.74) * mm});
            skLineSegment(sketch, "E345", {"start": v(-0.57, -2.74) * mm, "end": v(-0.65, -2.74) * mm});
            skLineSegment(sketch, "E346", {"start": v(-0.65, -2.74) * mm, "end": v(-0.73, -2.75) * mm});
            skLineSegment(sketch, "E347", {"start": v(-0.73, -2.75) * mm, "end": v(-0.82, -2.77) * mm});
            skLineSegment(sketch, "E348", {"start": v(-0.82, -2.77) * mm, "end": v(-0.92, -2.79) * mm});
            skLineSegment(sketch, "E349", {"start": v(-0.92, -2.79) * mm, "end": v(-1.05, -2.82) * mm});
            skLineSegment(sketch, "E350", {"start": v(-1.05, -2.82) * mm, "end": v(-1.17, -2.86) * mm});
            skLineSegment(sketch, "E351", {"start": v(-1.17, -2.86) * mm, "end": v(-1.29, -2.91) * mm});
            skLineSegment(sketch, "E352", {"start": v(-1.29, -2.91) * mm, "end": v(-1.4, -2.97) * mm});
            skLineSegment(sketch, "E353", {"start": v(-1.4, -2.97) * mm, "end": v(-1.5, -3.03) * mm});
            skLineSegment(sketch, "E354", {"start": v(-1.5, -3.03) * mm, "end": v(-1.6, -3.1) * mm});
            skLineSegment(sketch, "E355", {"start": v(-1.6, -3.1) * mm, "end": v(-1.7, -3.17) * mm});
            skLineSegment(sketch, "E356", {"start": v(-1.7, -3.17) * mm, "end": v(-1.79, -3.26) * mm});
            skLineSegment(sketch, "E357", {"start": v(-1.79, -3.26) * mm, "end": v(-1.87, -3.34) * mm});
            skLineSegment(sketch, "E358", {"start": v(-1.87, -3.34) * mm, "end": v(-1.95, -3.43) * mm});
            skLineSegment(sketch, "E359", {"start": v(-1.95, -3.43) * mm, "end": v(-2.02, -3.53) * mm});
            skLineSegment(sketch, "E360", {"start": v(-2.02, -3.53) * mm, "end": v(-2.08, -3.63) * mm});
            skLineSegment(sketch, "E361", {"start": v(-2.08, -3.63) * mm, "end": v(-2.14, -3.73) * mm});
            skLineSegment(sketch, "E362", {"start": v(-2.14, -3.73) * mm, "end": v(-2.19, -3.84) * mm});
            skLineSegment(sketch, "E363", {"start": v(-2.19, -3.84) * mm, "end": v(-2.23, -3.95) * mm});
            skLineSegment(sketch, "E364", {"start": v(-2.23, -3.95) * mm, "end": v(-2.26, -4.06) * mm});
            skLineSegment(sketch, "E365", {"start": v(-2.26, -4.06) * mm, "end": v(-2.3, -4.18) * mm});
            skLineSegment(sketch, "E366", {"start": v(-2.3, -4.18) * mm, "end": v(-2.32, -4.3) * mm});
            skLineSegment(sketch, "E367", {"start": v(-2.32, -4.3) * mm, "end": v(-2.33, -4.41) * mm});
            skLineSegment(sketch, "E368", {"start": v(-2.33, -4.41) * mm, "end": v(-2.34, -4.53) * mm});
            skLineSegment(sketch, "E369", {"start": v(-2.34, -4.53) * mm, "end": v(-2.34, -4.65) * mm});
            skLineSegment(sketch, "E370", {"start": v(-2.34, -4.65) * mm, "end": v(-2.33, -4.77) * mm});
            skLineSegment(sketch, "E371", {"start": v(-2.33, -4.77) * mm, "end": v(-2.31, -4.89) * mm});
            skLineSegment(sketch, "E372", {"start": v(-2.31, -4.89) * mm, "end": v(-2.3, -5) * mm});
            skLineSegment(sketch, "E373", {"start": v(-2.3, -5) * mm, "end": v(-2.26, -5.13) * mm});
            skLineSegment(sketch, "E374", {"start": v(-2.26, -5.13) * mm, "end": v(-2.22, -5.24) * mm});
            skLineSegment(sketch, "E375", {"start": v(-2.22, -5.24) * mm, "end": v(-2.17, -5.36) * mm});
            skLineSegment(sketch, "E376", {"start": v(-2.17, -5.36) * mm, "end": v(-2.12, -5.47) * mm});
            skLineSegment(sketch, "E377", {"start": v(-2.12, -5.47) * mm, "end": v(-2.05, -5.58) * mm});
            skLineSegment(sketch, "E378", {"start": v(-2.05, -5.58) * mm, "end": v(-1.98, -5.68) * mm});
            skLineSegment(sketch, "E379", {"start": v(-1.98, -5.68) * mm, "end": v(-1.9, -5.79) * mm});
            skLineSegment(sketch, "E380", {"start": v(-1.9, -5.79) * mm, "end": v(-1.8, -5.89) * mm});
            skLineSegment(sketch, "E381", {"start": v(-1.8, -5.89) * mm, "end": v(-1.75, -5.95) * mm});
            skLineSegment(sketch, "E382", {"start": v(-1.75, -5.95) * mm, "end": v(-1.68, -6) * mm});
            skLineSegment(sketch, "E383", {"start": v(-1.68, -6) * mm, "end": v(-1.62, -6.06) * mm});
            skLineSegment(sketch, "E384", {"start": v(-1.62, -6.06) * mm, "end": v(-1.55, -6.11) * mm});
            skLineSegment(sketch, "E385", {"start": v(-1.55, -6.11) * mm, "end": v(-1.49, -6.16) * mm});
            skLineSegment(sketch, "E386", {"start": v(-1.49, -6.16) * mm, "end": v(-1.42, -6.2) * mm});
            skLineSegment(sketch, "E387", {"start": v(-1.42, -6.2) * mm, "end": v(-1.35, -6.24) * mm});
            skLineSegment(sketch, "E388", {"start": v(-1.35, -6.24) * mm, "end": v(-1.28, -6.28) * mm});
            skLineSegment(sketch, "E389", {"start": v(-1.28, -6.28) * mm, "end": v(-1.22, -6.31) * mm});
            skLineSegment(sketch, "E390", {"start": v(-1.22, -6.31) * mm, "end": v(-1.15, -6.34) * mm});
            skLineSegment(sketch, "E391", {"start": v(-1.15, -6.34) * mm, "end": v(-1.08, -6.37) * mm});
            skLineSegment(sketch, "E392", {"start": v(-1.08, -6.37) * mm, "end": v(-1.01, -6.4) * mm});
            skLineSegment(sketch, "E393", {"start": v(-1.01, -6.4) * mm, "end": v(-0.95, -6.4) * mm});
            skLineSegment(sketch, "E394", {"start": v(-0.95, -6.4) * mm, "end": v(-0.88, -6.42) * mm});
            skLineSegment(sketch, "E395", {"start": v(-0.88, -6.42) * mm, "end": v(-0.82, -6.44) * mm});
            skLineSegment(sketch, "E396", {"start": v(-0.82, -6.44) * mm, "end": v(-0.76, -6.44) * mm});
            skLineSegment(sketch, "E397", {"start": v(-0.76, -6.44) * mm, "end": v(-0.7, -6.45) * mm});
            skLineSegment(sketch, "E398", {"start": v(-0.7, -6.45) * mm, "end": v(-0.64, -6.45) * mm});
            skLineSegment(sketch, "E399", {"start": v(-0.64, -6.45) * mm, "end": v(-0.58, -6.45) * mm});
            skLineSegment(sketch, "E400", {"start": v(-0.58, -6.45) * mm, "end": v(-0.53, -6.44) * mm});
            skLineSegment(sketch, "E401", {"start": v(-0.53, -6.44) * mm, "end": v(-0.47, -6.43) * mm});
            skLineSegment(sketch, "E402", {"start": v(-0.47, -6.43) * mm, "end": v(-0.43, -6.41) * mm});
            skLineSegment(sketch, "E403", {"start": v(-0.43, -6.41) * mm, "end": v(-0.38, -6.4) * mm});
            skLineSegment(sketch, "E404", {"start": v(-0.38, -6.4) * mm, "end": v(-0.34, -6.37) * mm});
            skLineSegment(sketch, "E405", {"start": v(-0.34, -6.37) * mm, "end": v(-0.3, -6.35) * mm});
            skLineSegment(sketch, "E406", {"start": v(-0.3, -6.35) * mm, "end": v(-0.27, -6.32) * mm});
            skLineSegment(sketch, "E407", {"start": v(-0.27, -6.32) * mm, "end": v(-0.24, -6.29) * mm});
            skLineSegment(sketch, "E408", {"start": v(-0.24, -6.29) * mm, "end": v(-0.2, -6.25) * mm});
            skLineSegment(sketch, "E409", {"start": v(-0.2, -6.25) * mm, "end": v(-0.19, -6.2) * mm});
            skLineSegment(sketch, "E410", {"start": v(-0.19, -6.2) * mm, "end": v(-0.17, -6.16) * mm});
            skLineSegment(sketch, "E411", {"start": v(-0.17, -6.16) * mm, "end": v(-0.16, -6.11) * mm});
            skLineSegment(sketch, "E412", {"start": v(-0.16, -6.11) * mm, "end": v(-0.15, -6.06) * mm});
            skLineSegment(sketch, "E413", {"start": v(-0.15, -6.06) * mm, "end": v(-0.12, -5.96) * mm});
            skLineSegment(sketch, "E414", {"start": v(-0.12, -5.96) * mm, "end": v(-0.09, -5.87) * mm});
            skLineSegment(sketch, "E415", {"start": v(-0.09, -5.87) * mm, "end": v(-0.05, -5.78) * mm});
            skLineSegment(sketch, "E416", {"start": v(-0.05, -5.78) * mm, "end": v(0, -5.7) * mm});
            skLineSegment(sketch, "E417", {"start": v(0, -5.7) * mm, "end": v(0.06, -5.62) * mm});
            skLineSegment(sketch, "E418", {"start": v(0.06, -5.62) * mm, "end": v(0.12, -5.54) * mm});
            skLineSegment(sketch, "E419", {"start": v(0.12, -5.54) * mm, "end": v(0.18, -5.47) * mm});
            skLineSegment(sketch, "E420", {"start": v(0.18, -5.47) * mm, "end": v(0.26, -5.4) * mm});
            skLineSegment(sketch, "E421", {"start": v(0.26, -5.4) * mm, "end": v(0.33, -5.35) * mm});
            skLineSegment(sketch, "E422", {"start": v(0.33, -5.35) * mm, "end": v(0.42, -5.3) * mm});
            skLineSegment(sketch, "E423", {"start": v(0.42, -5.3) * mm, "end": v(0.5, -5.26) * mm});
            skLineSegment(sketch, "E424", {"start": v(0.5, -5.26) * mm, "end": v(0.6, -5.22) * mm});
            skLineSegment(sketch, "E425", {"start": v(0.6, -5.22) * mm, "end": v(0.69, -5.19) * mm});
            skLineSegment(sketch, "E426", {"start": v(0.69, -5.19) * mm, "end": v(0.79, -5.17) * mm});
            skLineSegment(sketch, "E427", {"start": v(0.79, -5.17) * mm, "end": v(0.88, -5.15) * mm});
            skLineSegment(sketch, "E428", {"start": v(0.88, -5.15) * mm, "end": v(0.99, -5.15) * mm});
            skLineSegment(sketch, "E429", {"start": v(0.99, -5.15) * mm, "end": v(1.05, -5.15) * mm});
            skLineSegment(sketch, "E430", {"start": v(1.05, -5.15) * mm, "end": v(1.1, -5.16) * mm});
            skLineSegment(sketch, "E431", {"start": v(1.1, -5.16) * mm, "end": v(1.16, -5.16) * mm});
            skLineSegment(sketch, "E432", {"start": v(1.16, -5.16) * mm, "end": v(1.22, -5.17) * mm});
            skLineSegment(sketch, "E433", {"start": v(1.22, -5.17) * mm, "end": v(1.28, -5.19) * mm});
            skLineSegment(sketch, "E434", {"start": v(1.28, -5.19) * mm, "end": v(1.33, -5.2) * mm});
            skLineSegment(sketch, "E435", {"start": v(1.33, -5.2) * mm, "end": v(1.39, -5.22) * mm});
            skLineSegment(sketch, "E436", {"start": v(1.39, -5.22) * mm, "end": v(1.44, -5.24) * mm});
            skLineSegment(sketch, "E437", {"start": v(1.44, -5.24) * mm, "end": v(1.54, -5.3) * mm});
            skLineSegment(sketch, "E438", {"start": v(1.54, -5.3) * mm, "end": v(1.64, -5.35) * mm});
            skLineSegment(sketch, "E439", {"start": v(1.64, -5.35) * mm, "end": v(1.73, -5.42) * mm});
            skLineSegment(sketch, "E440", {"start": v(1.73, -5.42) * mm, "end": v(1.8, -5.5) * mm});
            skLineSegment(sketch, "E441", {"start": v(1.8, -5.5) * mm, "end": v(1.89, -5.57) * mm});
            skLineSegment(sketch, "E442", {"start": v(1.89, -5.57) * mm, "end": v(1.95, -5.66) * mm});
            skLineSegment(sketch, "E443", {"start": v(1.95, -5.66) * mm, "end": v(2.01, -5.76) * mm});
            skLineSegment(sketch, "E444", {"start": v(2.01, -5.76) * mm, "end": v(2.06, -5.86) * mm});
            skLineSegment(sketch, "E445", {"start": v(2.06, -5.86) * mm, "end": v(2.08, -5.91) * mm});
            skLineSegment(sketch, "E446", {"start": v(2.08, -5.91) * mm, "end": v(2.1, -5.97) * mm});
            skLineSegment(sketch, "E447", {"start": v(2.1, -5.97) * mm, "end": v(2.11, -6.02) * mm});
            skLineSegment(sketch, "E448", {"start": v(2.11, -6.02) * mm, "end": v(2.13, -6.08) * mm});
            skLineSegment(sketch, "E449", {"start": v(2.13, -6.08) * mm, "end": v(2.14, -6.14) * mm});
            skLineSegment(sketch, "E450", {"start": v(2.14, -6.14) * mm, "end": v(2.14, -6.2) * mm});
            skLineSegment(sketch, "E451", {"start": v(2.14, -6.2) * mm, "end": v(2.15, -6.25) * mm});
            skLineSegment(sketch, "E452", {"start": v(2.15, -6.25) * mm, "end": v(2.15, -6.31) * mm});
            skLineSegment(sketch, "E453", {"start": v(2.15, -6.31) * mm, "end": v(2.15, -6.37) * mm});
            skLineSegment(sketch, "E454", {"start": v(2.15, -6.37) * mm, "end": v(2.14, -6.43) * mm});
            skLineSegment(sketch, "E455", {"start": v(2.14, -6.43) * mm, "end": v(2.14, -6.5) * mm});
            skLineSegment(sketch, "E456", {"start": v(2.14, -6.5) * mm, "end": v(2.13, -6.55) * mm});
            skLineSegment(sketch, "E457", {"start": v(2.13, -6.55) * mm, "end": v(2.11, -6.6) * mm});
            skLineSegment(sketch, "E458", {"start": v(2.11, -6.6) * mm, "end": v(2.1, -6.66) * mm});
            skLineSegment(sketch, "E459", {"start": v(2.1, -6.66) * mm, "end": v(2.08, -6.72) * mm});
            skLineSegment(sketch, "E460", {"start": v(2.08, -6.72) * mm, "end": v(2.06, -6.77) * mm});
            skLineSegment(sketch, "E461", {"start": v(2.06, -6.77) * mm, "end": v(2.03, -6.82) * mm});
            skLineSegment(sketch, "E462", {"start": v(2.03, -6.82) * mm, "end": v(2, -6.87) * mm});
            skLineSegment(sketch, "E463", {"start": v(2, -6.87) * mm, "end": v(1.95, -6.97) * mm});
            skLineSegment(sketch, "E464", {"start": v(1.95, -6.97) * mm, "end": v(1.88, -7.06) * mm});
            skLineSegment(sketch, "E465", {"start": v(1.88, -7.06) * mm, "end": v(1.8, -7.15) * mm});
            skLineSegment(sketch, "E466", {"start": v(1.8, -7.15) * mm, "end": v(1.8, -7.15) * mm});
            skLineSegment(sketch, "E467", {"start": v(1.8, -7.15) * mm, "end": v(1.69, -7.3) * mm});
            skLineSegment(sketch, "E468", {"start": v(1.69, -7.3) * mm, "end": v(1.63, -7.38) * mm});
            skLineSegment(sketch, "E469", {"start": v(1.63, -7.38) * mm, "end": v(1.57, -7.45) * mm});
            skLineSegment(sketch, "E470", {"start": v(1.57, -7.45) * mm, "end": v(1.42, -7.64) * mm});
            skLineSegment(sketch, "E471", {"start": v(1.42, -7.64) * mm, "end": v(1.37, -7.72) * mm});
            skLineSegment(sketch, "E472", {"start": v(1.37, -7.72) * mm, "end": v(1.32, -7.79) * mm});
            skLineSegment(sketch, "E473", {"start": v(1.32, -7.79) * mm, "end": v(1.28, -7.85) * mm});
            skLineSegment(sketch, "E474", {"start": v(1.28, -7.85) * mm, "end": v(1.25, -7.9) * mm});
            skLineSegment(sketch, "E475", {"start": v(1.25, -7.9) * mm, "end": v(1.23, -7.96) * mm});
            skLineSegment(sketch, "E476", {"start": v(1.23, -7.96) * mm, "end": v(1.22, -8.01) * mm});
            skLineSegment(sketch, "E477", {"start": v(1.22, -8.01) * mm, "end": v(1.22, -8.06) * mm});
            skLineSegment(sketch, "E478", {"start": v(1.22, -8.06) * mm, "end": v(1.23, -8.11) * mm});
            skLineSegment(sketch, "E479", {"start": v(1.23, -8.11) * mm, "end": v(1.25, -8.16) * mm});
            skLineSegment(sketch, "E480", {"start": v(1.25, -8.16) * mm, "end": v(1.27, -8.21) * mm});
            skLineSegment(sketch, "E481", {"start": v(1.27, -8.21) * mm, "end": v(1.3, -8.26) * mm});
            skLineSegment(sketch, "E482", {"start": v(1.3, -8.26) * mm, "end": v(1.35, -8.32) * mm});
            skLineSegment(sketch, "E483", {"start": v(1.35, -8.32) * mm, "end": v(1.46, -8.46) * mm});
            skLineSegment(sketch, "E484", {"start": v(1.46, -8.46) * mm, "end": v(1.51, -8.52) * mm});
            skLineSegment(sketch, "E485", {"start": v(1.51, -8.52) * mm, "end": v(1.56, -8.58) * mm});
            skLineSegment(sketch, "E486", {"start": v(1.56, -8.58) * mm, "end": v(1.6, -8.65) * mm});
            skLineSegment(sketch, "E487", {"start": v(1.6, -8.65) * mm, "end": v(1.65, -8.72) * mm});
            skLineSegment(sketch, "E488", {"start": v(1.65, -8.72) * mm, "end": v(1.69, -8.8) * mm});
            skLineSegment(sketch, "E489", {"start": v(1.69, -8.8) * mm, "end": v(1.72, -8.88) * mm});
            skLineSegment(sketch, "E490", {"start": v(1.72, -8.88) * mm, "end": v(1.76, -8.96) * mm});
            skLineSegment(sketch, "E491", {"start": v(1.76, -8.96) * mm, "end": v(1.79, -9.05) * mm});
            skLineSegment(sketch, "E492", {"start": v(1.79, -9.05) * mm, "end": v(1.82, -9.14) * mm});
            skLineSegment(sketch, "E493", {"start": v(1.82, -9.14) * mm, "end": v(1.84, -9.23) * mm});
            skLineSegment(sketch, "E494", {"start": v(1.84, -9.23) * mm, "end": v(1.87, -9.33) * mm});
            skLineSegment(sketch, "E495", {"start": v(1.87, -9.33) * mm, "end": v(1.89, -9.42) * mm});
            skLineSegment(sketch, "E496", {"start": v(1.89, -9.42) * mm, "end": v(1.9, -9.52) * mm});
            skLineSegment(sketch, "E497", {"start": v(1.9, -9.52) * mm, "end": v(1.92, -9.62) * mm});
            skLineSegment(sketch, "E498", {"start": v(1.92, -9.62) * mm, "end": v(1.93, -9.72) * mm});
            skLineSegment(sketch, "E499", {"start": v(1.93, -9.72) * mm, "end": v(1.94, -9.82) * mm});
            skLineSegment(sketch, "E500", {"start": v(1.94, -9.82) * mm, "end": v(1.94, -9.92) * mm});
            skLineSegment(sketch, "E501", {"start": v(1.94, -9.92) * mm, "end": v(1.95, -10.02) * mm});
            skLineSegment(sketch, "E502", {"start": v(1.95, -10.02) * mm, "end": v(1.95, -10.12) * mm});
            skLineSegment(sketch, "E503", {"start": v(1.95, -10.12) * mm, "end": v(1.94, -10.22) * mm});
            skLineSegment(sketch, "E504", {"start": v(1.94, -10.22) * mm, "end": v(1.94, -10.33) * mm});
            skLineSegment(sketch, "E505", {"start": v(1.94, -10.33) * mm, "end": v(1.93, -10.43) * mm});
            skLineSegment(sketch, "E506", {"start": v(1.93, -10.43) * mm, "end": v(1.92, -10.53) * mm});
            skLineSegment(sketch, "E507", {"start": v(1.92, -10.53) * mm, "end": v(1.9, -10.63) * mm});
            skLineSegment(sketch, "E508", {"start": v(1.9, -10.63) * mm, "end": v(1.88, -10.72) * mm});
            skLineSegment(sketch, "E509", {"start": v(1.88, -10.72) * mm, "end": v(1.86, -10.82) * mm});
            skLineSegment(sketch, "E510", {"start": v(1.86, -10.82) * mm, "end": v(1.84, -10.91) * mm});
            skLineSegment(sketch, "E511", {"start": v(1.84, -10.91) * mm, "end": v(1.81, -11) * mm});
            skLineSegment(sketch, "E512", {"start": v(1.81, -11) * mm, "end": v(1.78, -11.1) * mm});
            skLineSegment(sketch, "E513", {"start": v(1.78, -11.1) * mm, "end": v(1.75, -11.18) * mm});
            skLineSegment(sketch, "E514", {"start": v(1.75, -11.18) * mm, "end": v(1.71, -11.27) * mm});
            skLineSegment(sketch, "E515", {"start": v(1.71, -11.27) * mm, "end": v(1.67, -11.35) * mm});
            skLineSegment(sketch, "E516", {"start": v(1.67, -11.35) * mm, "end": v(1.58, -11.53) * mm});
            skLineSegment(sketch, "E517", {"start": v(1.58, -11.53) * mm, "end": v(1.51, -11.67) * mm});
            skLineSegment(sketch, "E518", {"start": v(1.51, -11.67) * mm, "end": v(1.48, -11.74) * mm});
            skLineSegment(sketch, "E519", {"start": v(1.48, -11.74) * mm, "end": v(1.46, -11.8) * mm});
            skLineSegment(sketch, "E520", {"start": v(1.46, -11.8) * mm, "end": v(1.45, -11.86) * mm});
            skLineSegment(sketch, "E521", {"start": v(1.45, -11.86) * mm, "end": v(1.44, -11.9) * mm});
            skLineSegment(sketch, "E522", {"start": v(1.44, -11.9) * mm, "end": v(1.4, -12.22) * mm});
            skLineSegment(sketch, "E523", {"start": v(1.4, -12.22) * mm, "end": v(1.35, -12.67) * mm});
            skLineSegment(sketch, "E524", {"start": v(1.35, -12.67) * mm, "end": v(1.3, -13.21) * mm});
            skLineSegment(sketch, "E525", {"start": v(1.3, -13.21) * mm, "end": v(1.24, -13.82) * mm});
            skLineSegment(sketch, "E526", {"start": v(1.24, -13.82) * mm, "end": v(1.13, -15.18) * mm});
            skLineSegment(sketch, "E527", {"start": v(1.13, -15.18) * mm, "end": v(1.01, -16.62) * mm});
            skLineSegment(sketch, "E528", {"start": v(1.01, -16.62) * mm, "end": v(1.01, -16.87) * mm});
            skLineSegment(sketch, "E529", {"start": v(1.01, -16.87) * mm, "end": v(1.08, -16.92) * mm});
            skLineSegment(sketch, "E530", {"start": v(1.08, -16.92) * mm, "end": v(1.15, -16.98) * mm});
            skLineSegment(sketch, "E531", {"start": v(1.15, -16.98) * mm, "end": v(1.22, -17.04) * mm});
            skLineSegment(sketch, "E532", {"start": v(1.22, -17.04) * mm, "end": v(1.28, -17.1) * mm});
            skLineSegment(sketch, "E533", {"start": v(1.28, -17.1) * mm, "end": v(1.33, -17.17) * mm});
            skLineSegment(sketch, "E534", {"start": v(1.33, -17.17) * mm, "end": v(1.38, -17.24) * mm});
            skLineSegment(sketch, "E535", {"start": v(1.38, -17.24) * mm, "end": v(1.43, -17.32) * mm});
            skLineSegment(sketch, "E536", {"start": v(1.43, -17.32) * mm, "end": v(1.47, -17.4) * mm});
            skLineSegment(sketch, "E537", {"start": v(1.47, -17.4) * mm, "end": v(1.51, -17.47) * mm});
            skLineSegment(sketch, "E538", {"start": v(1.51, -17.47) * mm, "end": v(1.54, -17.56) * mm});
            skLineSegment(sketch, "E539", {"start": v(1.54, -17.56) * mm, "end": v(1.57, -17.64) * mm});
            skLineSegment(sketch, "E540", {"start": v(1.57, -17.64) * mm, "end": v(1.6, -17.72) * mm});
            skLineSegment(sketch, "E541", {"start": v(1.6, -17.72) * mm, "end": v(1.61, -17.81) * mm});
            skLineSegment(sketch, "E542", {"start": v(1.61, -17.81) * mm, "end": v(1.62, -17.9) * mm});
            skLineSegment(sketch, "E543", {"start": v(1.62, -17.9) * mm, "end": v(1.63, -17.99) * mm});
            skLineSegment(sketch, "E544", {"start": v(1.63, -17.99) * mm, "end": v(1.63, -18.07) * mm});
            skLineSegment(sketch, "E545", {"start": v(1.63, -18.07) * mm, "end": v(1.62, -18.16) * mm});
            skLineSegment(sketch, "E546", {"start": v(1.62, -18.16) * mm, "end": v(1.61, -18.25) * mm});
            skLineSegment(sketch, "E547", {"start": v(1.61, -18.25) * mm, "end": v(1.6, -18.33) * mm});
            skLineSegment(sketch, "E548", {"start": v(1.6, -18.33) * mm, "end": v(1.57, -18.42) * mm});
            skLineSegment(sketch, "E549", {"start": v(1.57, -18.42) * mm, "end": v(1.55, -18.5) * mm});
            skLineSegment(sketch, "E550", {"start": v(1.55, -18.5) * mm, "end": v(1.51, -18.59) * mm});
            skLineSegment(sketch, "E551", {"start": v(1.51, -18.59) * mm, "end": v(1.48, -18.67) * mm});
            skLineSegment(sketch, "E552", {"start": v(1.48, -18.67) * mm, "end": v(1.43, -18.74) * mm});
            skLineSegment(sketch, "E553", {"start": v(1.43, -18.74) * mm, "end": v(1.39, -18.82) * mm});
            skLineSegment(sketch, "E554", {"start": v(1.39, -18.82) * mm, "end": v(1.34, -18.89) * mm});
            skLineSegment(sketch, "E555", {"start": v(1.34, -18.89) * mm, "end": v(1.28, -18.96) * mm});
            skLineSegment(sketch, "E556", {"start": v(1.28, -18.96) * mm, "end": v(1.22, -19.02) * mm});
            skLineSegment(sketch, "E557", {"start": v(1.22, -19.02) * mm, "end": v(1.16, -19.08) * mm});
            skLineSegment(sketch, "E558", {"start": v(1.16, -19.08) * mm, "end": v(1.09, -19.14) * mm});
            skLineSegment(sketch, "E559", {"start": v(1.09, -19.14) * mm, "end": v(1.02, -19.19) * mm});
            skLineSegment(sketch, "E560", {"start": v(1.02, -19.19) * mm, "end": v(1.01, -19.2) * mm});
            skLineSegment(sketch, "E561", {"start": v(1.01, -19.2) * mm, "end": v(0.91, -20.83) * mm});
            skLineSegment(sketch, "E562", {"start": v(0.91, -20.83) * mm, "end": v(0.73, -31.33) * mm});
            skLineSegment(sketch, "E563", {"start": v(0.73, -31.33) * mm, "end": v(0.73, -31.35) * mm});
            skLineSegment(sketch, "E564", {"start": v(0.73, -31.35) * mm, "end": v(0.73, -31.37) * mm});
            skLineSegment(sketch, "E565", {"start": v(0.73, -31.37) * mm, "end": v(0.73, -31.39) * mm});
            skLineSegment(sketch, "E566", {"start": v(0.73, -31.39) * mm, "end": v(0.73, -31.4) * mm});
            skLineSegment(sketch, "E567", {"start": v(0.73, -31.4) * mm, "end": v(0.72, -31.43) * mm});
            skLineSegment(sketch, "E568", {"start": v(0.72, -31.43) * mm, "end": v(0.72, -31.45) * mm});
            skLineSegment(sketch, "E569", {"start": v(0.72, -31.45) * mm, "end": v(0.72, -31.46) * mm});
            skLineSegment(sketch, "E570", {"start": v(0.72, -31.46) * mm, "end": v(0.71, -31.48) * mm});
            skLineSegment(sketch, "E571", {"start": v(0.71, -31.48) * mm, "end": v(0.7, -31.5) * mm});
            skLineSegment(sketch, "E572", {"start": v(0.7, -31.5) * mm, "end": v(0.7, -31.52) * mm});
            skLineSegment(sketch, "E573", {"start": v(0.7, -31.52) * mm, "end": v(0.7, -31.54) * mm});
            skLineSegment(sketch, "E574", {"start": v(0.7, -31.54) * mm, "end": v(0.69, -31.56) * mm});
            skLineSegment(sketch, "E575", {"start": v(0.69, -31.56) * mm, "end": v(0.68, -31.57) * mm});
            skLineSegment(sketch, "E576", {"start": v(0.68, -31.57) * mm, "end": v(0.67, -31.6) * mm});
            skLineSegment(sketch, "E577", {"start": v(0.67, -31.6) * mm, "end": v(0.67, -31.6) * mm});
            skLineSegment(sketch, "E578", {"start": v(0.67, -31.6) * mm, "end": v(0.66, -31.63) * mm});
            skLineSegment(sketch, "E579", {"start": v(0.66, -31.63) * mm, "end": v(0.65, -31.64) * mm});
            skLineSegment(sketch, "E580", {"start": v(0.65, -31.64) * mm, "end": v(0.64, -31.66) * mm});
            skLineSegment(sketch, "E581", {"start": v(0.64, -31.66) * mm, "end": v(0.63, -31.67) * mm});
            skLineSegment(sketch, "E582", {"start": v(0.63, -31.67) * mm, "end": v(0.62, -31.7) * mm});
            skLineSegment(sketch, "E583", {"start": v(0.62, -31.7) * mm, "end": v(0.6, -31.7) * mm});
            skLineSegment(sketch, "E584", {"start": v(0.6, -31.7) * mm, "end": v(0.6, -31.72) * mm});
            skLineSegment(sketch, "E585", {"start": v(0.6, -31.72) * mm, "end": v(0.58, -31.74) * mm});
            skLineSegment(sketch, "E586", {"start": v(0.58, -31.74) * mm, "end": v(0.57, -31.75) * mm});
            skLineSegment(sketch, "E587", {"start": v(0.57, -31.75) * mm, "end": v(0.55, -31.76) * mm});
            skLineSegment(sketch, "E588", {"start": v(0.55, -31.76) * mm, "end": v(0.54, -31.78) * mm});
            skLineSegment(sketch, "E589", {"start": v(0.54, -31.78) * mm, "end": v(0.53, -31.8) * mm});
            skLineSegment(sketch, "E590", {"start": v(0.53, -31.8) * mm, "end": v(0.51, -31.8) * mm});
            skLineSegment(sketch, "E591", {"start": v(0.51, -31.8) * mm, "end": v(0.5, -31.81) * mm});
            skLineSegment(sketch, "E592", {"start": v(0.5, -31.81) * mm, "end": v(0.48, -31.83) * mm});
            skLineSegment(sketch, "E593", {"start": v(0.48, -31.83) * mm, "end": v(0.47, -31.84) * mm});
            skLineSegment(sketch, "E594", {"start": v(0.47, -31.84) * mm, "end": v(0.45, -31.85) * mm});
            skLineSegment(sketch, "E595", {"start": v(0.45, -31.85) * mm, "end": v(0.43, -31.86) * mm});
            skLineSegment(sketch, "E596", {"start": v(0.43, -31.86) * mm, "end": v(0.42, -31.87) * mm});
            skLineSegment(sketch, "E597", {"start": v(0.42, -31.87) * mm, "end": v(0.4, -31.88) * mm});
            skLineSegment(sketch, "E598", {"start": v(0.4, -31.88) * mm, "end": v(0.38, -31.89) * mm});
            skLineSegment(sketch, "E599", {"start": v(0.38, -31.89) * mm, "end": v(0.37, -31.9) * mm});
            skLineSegment(sketch, "E600", {"start": v(0.37, -31.9) * mm, "end": v(0.35, -31.9) * mm});
            skLineSegment(sketch, "E601", {"start": v(0.35, -31.9) * mm, "end": v(0.33, -31.9) * mm});
            skLineSegment(sketch, "E602", {"start": v(0.33, -31.9) * mm, "end": v(0.31, -31.91) * mm});
            skLineSegment(sketch, "E603", {"start": v(0.31, -31.91) * mm, "end": v(0.3, -31.92) * mm});
            skLineSegment(sketch, "E604", {"start": v(0.3, -31.92) * mm, "end": v(0.28, -31.92) * mm});
            skLineSegment(sketch, "E605", {"start": v(0.28, -31.92) * mm, "end": v(0.26, -31.93) * mm});
            skLineSegment(sketch, "E606", {"start": v(0.26, -31.93) * mm, "end": v(0.24, -31.93) * mm});
            skLineSegment(sketch, "E607", {"start": v(0.24, -31.93) * mm, "end": v(0.22, -31.94) * mm});
            skLineSegment(sketch, "E608", {"start": v(0.22, -31.94) * mm, "end": v(0.2, -31.94) * mm});
            skLineSegment(sketch, "E609", {"start": v(0.2, -31.94) * mm, "end": v(0.18, -31.94) * mm});
            skLineSegment(sketch, "E610", {"start": v(0.18, -31.94) * mm, "end": v(0.16, -31.94) * mm});
            skLineSegment(sketch, "E611", {"start": v(0.16, -31.94) * mm, "end": v(0.14, -31.94) * mm});
            skLineSegment(sketch, "E612", {"start": v(0.14, -31.94) * mm, "end": v(0.12, -31.94) * mm});
            skLineSegment(sketch, "E613", {"start": v(0.12, -31.94) * mm, "end": v(0.1, -31.94) * mm});
            skLineSegment(sketch, "E614", {"start": v(0.1, -31.94) * mm, "end": v(0.09, -31.94) * mm});
            skLineSegment(sketch, "E615", {"start": v(0.09, -31.94) * mm, "end": v(0.07, -31.94) * mm});
            skLineSegment(sketch, "E616", {"start": v(0.07, -31.94) * mm, "end": v(0.05, -31.94) * mm});
            skLineSegment(sketch, "E617", {"start": v(0.05, -31.94) * mm, "end": v(0.03, -31.94) * mm});
            skLineSegment(sketch, "E618", {"start": v(0.03, -31.94) * mm, "end": v(0.01, -31.93) * mm});
            skLineSegment(sketch, "E619", {"start": v(0.01, -31.93) * mm, "end": v(0, -31.93) * mm});
            skLineSegment(sketch, "E620", {"start": v(0, -31.93) * mm, "end": v(-0.03, -31.93) * mm});
            skLineSegment(sketch, "E621", {"start": v(-0.03, -31.93) * mm, "end": v(-0.05, -31.92) * mm});
            skLineSegment(sketch, "E622", {"start": v(-0.05, -31.92) * mm, "end": v(-0.06, -31.92) * mm});
            skLineSegment(sketch, "E623", {"start": v(-0.06, -31.92) * mm, "end": v(-0.08, -31.9) * mm});
            skLineSegment(sketch, "E624", {"start": v(-0.08, -31.9) * mm, "end": v(-0.1, -31.9) * mm});
            skLineSegment(sketch, "E625", {"start": v(-0.1, -31.9) * mm, "end": v(-0.12, -31.9) * mm});
            skLineSegment(sketch, "E626", {"start": v(-0.12, -31.9) * mm, "end": v(-0.13, -31.89) * mm});
            skLineSegment(sketch, "E627", {"start": v(-0.13, -31.89) * mm, "end": v(-0.15, -31.88) * mm});
            skLineSegment(sketch, "E628", {"start": v(-0.15, -31.88) * mm, "end": v(-0.17, -31.87) * mm});
            skLineSegment(sketch, "E629", {"start": v(-0.17, -31.87) * mm, "end": v(-0.19, -31.86) * mm});
            skLineSegment(sketch, "E630", {"start": v(-0.19, -31.86) * mm, "end": v(-0.2, -31.85) * mm});
            skLineSegment(sketch, "E631", {"start": v(-0.2, -31.85) * mm, "end": v(-0.22, -31.84) * mm});
            skLineSegment(sketch, "E632", {"start": v(-0.22, -31.84) * mm, "end": v(-0.23, -31.83) * mm});
            skLineSegment(sketch, "E633", {"start": v(-0.23, -31.83) * mm, "end": v(-0.25, -31.82) * mm});
            skLineSegment(sketch, "E634", {"start": v(-0.25, -31.82) * mm, "end": v(-0.26, -31.8) * mm});
            skLineSegment(sketch, "E635", {"start": v(-0.26, -31.8) * mm, "end": v(-0.28, -31.8) * mm});
            skLineSegment(sketch, "E636", {"start": v(-0.28, -31.8) * mm, "end": v(-0.3, -31.78) * mm});
            skLineSegment(sketch, "E637", {"start": v(-0.3, -31.78) * mm, "end": v(-0.3, -31.77) * mm});
            skLineSegment(sketch, "E638", {"start": v(-0.3, -31.77) * mm, "end": v(-0.32, -31.76) * mm});
            skLineSegment(sketch, "E639", {"start": v(-0.32, -31.76) * mm, "end": v(-0.33, -31.74) * mm});
            skLineSegment(sketch, "E640", {"start": v(-0.33, -31.74) * mm, "end": v(-0.35, -31.73) * mm});
            skLineSegment(sketch, "E641", {"start": v(-0.35, -31.73) * mm, "end": v(-0.36, -31.71) * mm});
            skLineSegment(sketch, "E642", {"start": v(-0.36, -31.71) * mm, "end": v(-0.37, -31.7) * mm});
            skLineSegment(sketch, "E643", {"start": v(-0.37, -31.7) * mm, "end": v(-0.38, -31.68) * mm});
            skLineSegment(sketch, "E644", {"start": v(-0.38, -31.68) * mm, "end": v(-0.4, -31.67) * mm});
            skLineSegment(sketch, "E645", {"start": v(-0.4, -31.67) * mm, "end": v(-0.4, -31.65) * mm});
            skLineSegment(sketch, "E646", {"start": v(-0.4, -31.65) * mm, "end": v(-0.41, -31.63) * mm});
            skLineSegment(sketch, "E647", {"start": v(-0.41, -31.63) * mm, "end": v(-0.42, -31.62) * mm});
            skLineSegment(sketch, "E648", {"start": v(-0.42, -31.62) * mm, "end": v(-0.43, -31.6) * mm});
            skLineSegment(sketch, "E649", {"start": v(-0.43, -31.6) * mm, "end": v(-0.44, -31.58) * mm});
            skLineSegment(sketch, "E650", {"start": v(-0.44, -31.58) * mm, "end": v(-0.44, -31.56) * mm});
            skLineSegment(sketch, "E651", {"start": v(-0.44, -31.56) * mm, "end": v(-0.45, -31.55) * mm});
            skLineSegment(sketch, "E652", {"start": v(-0.45, -31.55) * mm, "end": v(-0.46, -31.53) * mm});
            skLineSegment(sketch, "E653", {"start": v(-0.46, -31.53) * mm, "end": v(-0.46, -31.5) * mm});
            skLineSegment(sketch, "E654", {"start": v(-0.46, -31.5) * mm, "end": v(-0.47, -31.5) * mm});
            skLineSegment(sketch, "E655", {"start": v(-0.47, -31.5) * mm, "end": v(-0.47, -31.47) * mm});
            skLineSegment(sketch, "E656", {"start": v(-0.47, -31.47) * mm, "end": v(-0.48, -31.45) * mm});
            skLineSegment(sketch, "E657", {"start": v(-0.48, -31.45) * mm, "end": v(-0.48, -31.43) * mm});
            skLineSegment(sketch, "E658", {"start": v(-0.48, -31.43) * mm, "end": v(-0.48, -31.42) * mm});
            skLineSegment(sketch, "E659", {"start": v(-0.48, -31.42) * mm, "end": v(-0.48, -31.4) * mm});
            skLineSegment(sketch, "E660", {"start": v(-0.48, -31.4) * mm, "end": v(-0.49, -31.38) * mm});
            skLineSegment(sketch, "E661", {"start": v(-0.49, -31.38) * mm, "end": v(-0.49, -31.36) * mm});
            skLineSegment(sketch, "E662", {"start": v(-0.49, -31.36) * mm, "end": v(-0.8, -20.94) * mm});
            skLineSegment(sketch, "E663", {"start": v(-0.8, -20.94) * mm, "end": v(-0.8, -19.6) * mm});
            skLineSegment(sketch, "E664", {"start": v(-0.8, -19.6) * mm, "end": v(-0.81, -18.97) * mm});
            skLineSegment(sketch, "E665", {"start": v(-0.81, -18.97) * mm, "end": v(-0.87, -18.9) * mm});
            skLineSegment(sketch, "E666", {"start": v(-0.87, -18.9) * mm, "end": v(-0.92, -18.83) * mm});
            skLineSegment(sketch, "E667", {"start": v(-0.92, -18.83) * mm, "end": v(-0.97, -18.76) * mm});
            skLineSegment(sketch, "E668", {"start": v(-0.97, -18.76) * mm, "end": v(-1.01, -18.68) * mm});
            skLineSegment(sketch, "E669", {"start": v(-1.01, -18.68) * mm, "end": v(-1.05, -18.6) * mm});
            skLineSegment(sketch, "E670", {"start": v(-1.05, -18.6) * mm, "end": v(-1.08, -18.52) * mm});
            skLineSegment(sketch, "E671", {"start": v(-1.08, -18.52) * mm, "end": v(-1.11, -18.44) * mm});
            skLineSegment(sketch, "E672", {"start": v(-1.11, -18.44) * mm, "end": v(-1.13, -18.35) * mm});
            skLineSegment(sketch, "E673", {"start": v(-1.13, -18.35) * mm, "end": v(-1.15, -18.27) * mm});
            skLineSegment(sketch, "E674", {"start": v(-1.15, -18.27) * mm, "end": v(-1.16, -18.18) * mm});
            skLineSegment(sketch, "E675", {"start": v(-1.16, -18.18) * mm, "end": v(-1.17, -18.1) * mm});
            skLineSegment(sketch, "E676", {"start": v(-1.17, -18.1) * mm, "end": v(-1.17, -18) * mm});
            skLineSegment(sketch, "E677", {"start": v(-1.17, -18) * mm, "end": v(-1.17, -17.92) * mm});
            skLineSegment(sketch, "E678", {"start": v(-1.17, -17.92) * mm, "end": v(-1.16, -17.83) * mm});
            skLineSegment(sketch, "E679", {"start": v(-1.16, -17.83) * mm, "end": v(-1.14, -17.74) * mm});
            skLineSegment(sketch, "E680", {"start": v(-1.14, -17.74) * mm, "end": v(-1.12, -17.66) * mm});
            skLineSegment(sketch, "E681", {"start": v(-1.12, -17.66) * mm, "end": v(-1.1, -17.57) * mm});
            skLineSegment(sketch, "E682", {"start": v(-1.1, -17.57) * mm, "end": v(-1.06, -17.5) * mm});
            skLineSegment(sketch, "E683", {"start": v(-1.06, -17.5) * mm, "end": v(-1.03, -17.41) * mm});
            skLineSegment(sketch, "E684", {"start": v(-1.03, -17.41) * mm, "end": v(-0.99, -17.33) * mm});
            skLineSegment(sketch, "E685", {"start": v(-0.99, -17.33) * mm, "end": v(-0.94, -17.26) * mm});
            skLineSegment(sketch, "E686", {"start": v(-0.94, -17.26) * mm, "end": v(-0.89, -17.19) * mm});
            skLineSegment(sketch, "E687", {"start": v(-0.89, -17.19) * mm, "end": v(-0.83, -17.12) * mm});
            skLineSegment(sketch, "E688", {"start": v(-0.83, -17.12) * mm, "end": v(-0.81, -17.1) * mm});
            skLineSegment(sketch, "E689", {"start": v(-0.81, -17.1) * mm, "end": v(-0.82, -15.44) * mm});
            skLineSegment(sketch, "E690", {"start": v(-0.82, -15.44) * mm, "end": v(-0.83, -14.78) * mm});
            skLineSegment(sketch, "E691", {"start": v(-0.83, -14.78) * mm, "end": v(-0.84, -14.17) * mm});
            skLineSegment(sketch, "E692", {"start": v(-0.84, -14.17) * mm, "end": v(-0.85, -13.6) * mm});
            skLineSegment(sketch, "E693", {"start": v(-0.85, -13.6) * mm, "end": v(-0.87, -13.1) * mm});
            skLineSegment(sketch, "E694", {"start": v(-0.87, -13.1) * mm, "end": v(-0.89, -12.7) * mm});
            skLineSegment(sketch, "E695", {"start": v(-0.89, -12.7) * mm, "end": v(-0.9, -12.38) * mm});
            skLineSegment(sketch, "E696", {"start": v(-0.9, -12.38) * mm, "end": v(-0.92, -12.3) * mm});
            skLineSegment(sketch, "E697", {"start": v(-0.92, -12.3) * mm, "end": v(-0.94, -12.22) * mm});
            skLineSegment(sketch, "E698", {"start": v(-0.94, -12.22) * mm, "end": v(-0.97, -12.15) * mm});
            skLineSegment(sketch, "E699", {"start": v(-0.97, -12.15) * mm, "end": v(-1, -12.09) * mm});
            skLineSegment(sketch, "E700", {"start": v(-1, -12.09) * mm, "end": v(-1.03, -12.03) * mm});
            skLineSegment(sketch, "E701", {"start": v(-1.03, -12.03) * mm, "end": v(-1.07, -11.97) * mm});
            skLineSegment(sketch, "E702", {"start": v(-1.07, -11.97) * mm, "end": v(-1.12, -11.92) * mm});
            skLineSegment(sketch, "E703", {"start": v(-1.12, -11.92) * mm, "end": v(-1.16, -11.87) * mm});
            skLineSegment(sketch, "E704", {"start": v(-1.16, -11.87) * mm, "end": v(-1.26, -11.79) * mm});
            skLineSegment(sketch, "E705", {"start": v(-1.26, -11.79) * mm, "end": v(-1.36, -11.7) * mm});
            skLineSegment(sketch, "E706", {"start": v(-1.36, -11.7) * mm, "end": v(-1.45, -11.62) * mm});
            skLineSegment(sketch, "E707", {"start": v(-1.45, -11.62) * mm, "end": v(-1.5, -11.58) * mm});
            skLineSegment(sketch, "E708", {"start": v(-1.5, -11.58) * mm, "end": v(-1.54, -11.54) * mm});
            skLineSegment(sketch, "E709", {"start": v(-1.54, -11.54) * mm, "end": v(-1.54, -11.54) * mm});
            skLineSegment(sketch, "E710", {"start": v(-1.54, -11.54) * mm, "end": v(-1.69, -11.42) * mm});
            skLineSegment(sketch, "E711", {"start": v(-1.69, -11.42) * mm, "end": v(-1.76, -11.36) * mm});
            skLineSegment(sketch, "E712", {"start": v(-1.76, -11.36) * mm, "end": v(-1.82, -11.3) * mm});
            skLineSegment(sketch, "E713", {"start": v(-1.82, -11.3) * mm, "end": v(-1.88, -11.25) * mm});
            skLineSegment(sketch, "E714", {"start": v(-1.88, -11.25) * mm, "end": v(-1.94, -11.19) * mm});
            skLineSegment(sketch, "E715", {"start": v(-1.94, -11.19) * mm, "end": v(-2, -11.12) * mm});
            skLineSegment(sketch, "E716", {"start": v(-2, -11.12) * mm, "end": v(-2.04, -11.06) * mm});
            skLineSegment(sketch, "E717", {"start": v(-2.04, -11.06) * mm, "end": v(-2.08, -11) * mm});
            skLineSegment(sketch, "E718", {"start": v(-2.08, -11) * mm, "end": v(-2.12, -10.93) * mm});
            skLineSegment(sketch, "E719", {"start": v(-2.12, -10.93) * mm, "end": v(-2.15, -10.86) * mm});
            skLineSegment(sketch, "E720", {"start": v(-2.15, -10.86) * mm, "end": v(-2.17, -10.79) * mm});
            skLineSegment(sketch, "E721", {"start": v(-2.17, -10.79) * mm, "end": v(-2.2, -10.71) * mm});
            skLineSegment(sketch, "E722", {"start": v(-2.2, -10.71) * mm, "end": v(-2.2, -10.63) * mm});
            skLineSegment(sketch, "E723", {"start": v(-2.2, -10.63) * mm, "end": v(-2.22, -10.55) * mm});
            skLineSegment(sketch, "E724", {"start": v(-2.22, -10.55) * mm, "end": v(-2.22, -10.46) * mm});
            skLineSegment(sketch, "E725", {"start": v(-2.22, -10.46) * mm, "end": v(-2.22, -10.4) * mm});
            skLineSegment(sketch, "E726", {"start": v(-2.22, -10.4) * mm, "end": v(-2.21, -10.34) * mm});
            skLineSegment(sketch, "E727", {"start": v(-2.21, -10.34) * mm, "end": v(-2.2, -10.28) * mm});
            skLineSegment(sketch, "E728", {"start": v(-2.2, -10.28) * mm, "end": v(-2.2, -10.22) * mm});
            skLineSegment(sketch, "E729", {"start": v(-2.2, -10.22) * mm, "end": v(-2.18, -10.17) * mm});
            skLineSegment(sketch, "E730", {"start": v(-2.18, -10.17) * mm, "end": v(-2.17, -10.1) * mm});
            skLineSegment(sketch, "E731", {"start": v(-2.17, -10.1) * mm, "end": v(-2.15, -10.05) * mm});
            skLineSegment(sketch, "E732", {"start": v(-2.15, -10.05) * mm, "end": v(-2.13, -10) * mm});
            skLineSegment(sketch, "E733", {"start": v(-2.13, -10) * mm, "end": v(-2.1, -9.95) * mm});
            skLineSegment(sketch, "E734", {"start": v(-2.1, -9.95) * mm, "end": v(-2.08, -9.9) * mm});
            skLineSegment(sketch, "E735", {"start": v(-2.08, -9.9) * mm, "end": v(-2.02, -9.8) * mm});
            skLineSegment(sketch, "E736", {"start": v(-2.02, -9.8) * mm, "end": v(-1.95, -9.7) * mm});
            skLineSegment(sketch, "E737", {"start": v(-1.95, -9.7) * mm, "end": v(-1.87, -9.62) * mm});
            skLineSegment(sketch, "E738", {"start": v(-1.87, -9.62) * mm, "end": v(-1.79, -9.55) * mm});
            skLineSegment(sketch, "E739", {"start": v(-1.79, -9.55) * mm, "end": v(-1.7, -9.48) * mm});
            skLineSegment(sketch, "E740", {"start": v(-1.7, -9.48) * mm, "end": v(-1.6, -9.42) * mm});
            skLineSegment(sketch, "E741", {"start": v(-1.6, -9.42) * mm, "end": v(-1.55, -9.4) * mm});
            skLineSegment(sketch, "E742", {"start": v(-1.55, -9.4) * mm, "end": v(-1.5, -9.37) * mm});
            skLineSegment(sketch, "E743", {"start": v(-1.5, -9.37) * mm, "end": v(-1.44, -9.35) * mm});
            skLineSegment(sketch, "E744", {"start": v(-1.44, -9.35) * mm, "end": v(-1.39, -9.33) * mm});
            skLineSegment(sketch, "E745", {"start": v(-1.39, -9.33) * mm, "end": v(-1.33, -9.31) * mm});
            skLineSegment(sketch, "E746", {"start": v(-1.33, -9.31) * mm, "end": v(-1.27, -9.3) * mm});
            skLineSegment(sketch, "E747", {"start": v(-1.27, -9.3) * mm, "end": v(-1.21, -9.29) * mm});
            skLineSegment(sketch, "E748", {"start": v(-1.21, -9.29) * mm, "end": v(-1.15, -9.28) * mm});
            skLineSegment(sketch, "E749", {"start": v(-1.15, -9.28) * mm, "end": v(-1.1, -9.28) * mm});
            skLineSegment(sketch, "E750", {"start": v(-1.1, -9.28) * mm, "end": v(-1.03, -9.27) * mm});
            skLineSegment(sketch, "E751", {"start": v(-1.03, -9.27) * mm, "end": v(-0.97, -9.28) * mm});
            skLineSegment(sketch, "E752", {"start": v(-0.97, -9.28) * mm, "end": v(-0.91, -9.28) * mm});
            skLineSegment(sketch, "E753", {"start": v(-0.91, -9.28) * mm, "end": v(-0.85, -9.29) * mm});
            skLineSegment(sketch, "E754", {"start": v(-0.85, -9.29) * mm, "end": v(-0.8, -9.3) * mm});
            skLineSegment(sketch, "E755", {"start": v(-0.8, -9.3) * mm, "end": v(-0.74, -9.31) * mm});
            skLineSegment(sketch, "E756", {"start": v(-0.74, -9.31) * mm, "end": v(-0.68, -9.33) * mm});
            skLineSegment(sketch, "E757", {"start": v(-0.68, -9.33) * mm, "end": v(-0.62, -9.35) * mm});
            skLineSegment(sketch, "E758", {"start": v(-0.62, -9.35) * mm, "end": v(-0.57, -9.37) * mm});
            skLineSegment(sketch, "E759", {"start": v(-0.57, -9.37) * mm, "end": v(-0.52, -9.4) * mm});
            skLineSegment(sketch, "E760", {"start": v(-0.52, -9.4) * mm, "end": v(-0.47, -9.42) * mm});
            skLineSegment(sketch, "E761", {"start": v(-0.47, -9.42) * mm, "end": v(-0.37, -9.48) * mm});
            skLineSegment(sketch, "E762", {"start": v(-0.37, -9.48) * mm, "end": v(-0.28, -9.55) * mm});
            skLineSegment(sketch, "E763", {"start": v(-0.28, -9.55) * mm, "end": v(-0.2, -9.62) * mm});
            skLineSegment(sketch, "E764", {"start": v(-0.2, -9.62) * mm, "end": v(-0.12, -9.7) * mm});
            skLineSegment(sketch, "E765", {"start": v(-0.12, -9.7) * mm, "end": v(-0.05, -9.8) * mm});
            skLineSegment(sketch, "E766", {"start": v(-0.05, -9.8) * mm, "end": v(0.01, -9.9) * mm});
            skLineSegment(sketch, "E767", {"start": v(0.01, -9.9) * mm, "end": v(0.04, -9.95) * mm});
            skLineSegment(sketch, "E768", {"start": v(0.04, -9.95) * mm, "end": v(0.06, -10) * mm});
            skLineSegment(sketch, "E769", {"start": v(0.06, -10) * mm, "end": v(0.08, -10.05) * mm});
            skLineSegment(sketch, "E770", {"start": v(0.08, -10.05) * mm, "end": v(0.1, -10.1) * mm});
            skLineSegment(sketch, "E771", {"start": v(0.1, -10.1) * mm, "end": v(0.12, -10.17) * mm});
            skLineSegment(sketch, "E772", {"start": v(0.12, -10.17) * mm, "end": v(0.13, -10.22) * mm});
            skLineSegment(sketch, "E773", {"start": v(0.13, -10.22) * mm, "end": v(0.14, -10.28) * mm});
            skLineSegment(sketch, "E774", {"start": v(0.14, -10.28) * mm, "end": v(0.15, -10.34) * mm});
            skLineSegment(sketch, "E775", {"start": v(0.15, -10.34) * mm, "end": v(0.15, -10.4) * mm});
            skLineSegment(sketch, "E776", {"start": v(0.15, -10.4) * mm, "end": v(0.16, -10.46) * mm});
            skLineSegment(sketch, "E777", {"start": v(0.16, -10.46) * mm, "end": v(0.15, -10.54) * mm});
            skLineSegment(sketch, "E778", {"start": v(0.15, -10.54) * mm, "end": v(0.15, -10.62) * mm});
            skLineSegment(sketch, "E779", {"start": v(0.15, -10.62) * mm, "end": v(0.13, -10.7) * mm});
            skLineSegment(sketch, "E780", {"start": v(0.13, -10.7) * mm, "end": v(0.12, -10.77) * mm});
            skLineSegment(sketch, "E781", {"start": v(0.12, -10.77) * mm, "end": v(0.1, -10.84) * mm});
            skLineSegment(sketch, "E782", {"start": v(0.1, -10.84) * mm, "end": v(0.07, -10.91) * mm});
            skLineSegment(sketch, "E783", {"start": v(0.07, -10.91) * mm, "end": v(0.04, -10.98) * mm});
            skLineSegment(sketch, "E784", {"start": v(0.04, -10.98) * mm, "end": v(0, -11.05) * mm});
            skLineSegment(sketch, "E785", {"start": v(0, -11.05) * mm, "end": v(0.03, -11.05) * mm});
            skLineSegment(sketch, "E786", {"start": v(0.03, -11.05) * mm, "end": v(0.07, -11.04) * mm});
            skLineSegment(sketch, "E787", {"start": v(0.07, -11.04) * mm, "end": v(0.17, -11) * mm});
            skLineSegment(sketch, "E788", {"start": v(0.17, -11) * mm, "end": v(0.3, -10.95) * mm});
            skLineSegment(sketch, "E789", {"start": v(0.3, -10.95) * mm, "end": v(0.44, -10.87) * mm});
            skLineSegment(sketch, "E790", {"start": v(0.44, -10.87) * mm, "end": v(0.5, -10.84) * mm});
            skLineSegment(sketch, "E791", {"start": v(0.5, -10.84) * mm, "end": v(0.55, -10.8) * mm});
            skLineSegment(sketch, "E792", {"start": v(0.55, -10.8) * mm, "end": v(0.6, -10.76) * mm});
            skLineSegment(sketch, "E793", {"start": v(0.6, -10.76) * mm, "end": v(0.65, -10.72) * mm});
            skLineSegment(sketch, "E794", {"start": v(0.65, -10.72) * mm, "end": v(0.69, -10.67) * mm});
            skLineSegment(sketch, "E795", {"start": v(0.69, -10.67) * mm, "end": v(0.72, -10.62) * mm});
            skLineSegment(sketch, "E796", {"start": v(0.72, -10.62) * mm, "end": v(0.76, -10.57) * mm});
            skLineSegment(sketch, "E797", {"start": v(0.76, -10.57) * mm, "end": v(0.79, -10.51) * mm});
            skLineSegment(sketch, "E798", {"start": v(0.79, -10.51) * mm, "end": v(0.81, -10.45) * mm});
            skLineSegment(sketch, "E799", {"start": v(0.81, -10.45) * mm, "end": v(0.84, -10.4) * mm});
            skLineSegment(sketch, "E800", {"start": v(0.84, -10.4) * mm, "end": v(0.85, -10.33) * mm});
            skLineSegment(sketch, "E801", {"start": v(0.85, -10.33) * mm, "end": v(0.87, -10.26) * mm});
            skLineSegment(sketch, "E802", {"start": v(0.87, -10.26) * mm, "end": v(0.88, -10.2) * mm});
            skLineSegment(sketch, "E803", {"start": v(0.88, -10.2) * mm, "end": v(0.88, -10.12) * mm});
            skLineSegment(sketch, "E804", {"start": v(0.88, -10.12) * mm, "end": v(0.89, -10.05) * mm});
            skLineSegment(sketch, "E805", {"start": v(0.89, -10.05) * mm, "end": v(0.89, -9.97) * mm});
            skLineSegment(sketch, "E806", {"start": v(0.89, -9.97) * mm, "end": v(0.88, -9.9) * mm});
            skLineSegment(sketch, "E807", {"start": v(0.88, -9.9) * mm, "end": v(0.87, -9.82) * mm});
            skLineSegment(sketch, "E808", {"start": v(0.87, -9.82) * mm, "end": v(0.86, -9.74) * mm});
            skLineSegment(sketch, "E809", {"start": v(0.86, -9.74) * mm, "end": v(0.84, -9.66) * mm});
            skLineSegment(sketch, "E810", {"start": v(0.84, -9.66) * mm, "end": v(0.82, -9.58) * mm});
            skLineSegment(sketch, "E811", {"start": v(0.82, -9.58) * mm, "end": v(0.8, -9.5) * mm});
            skLineSegment(sketch, "E812", {"start": v(0.8, -9.5) * mm, "end": v(0.77, -9.42) * mm});
            skLineSegment(sketch, "E813", {"start": v(0.77, -9.42) * mm, "end": v(0.74, -9.34) * mm});
            skLineSegment(sketch, "E814", {"start": v(0.74, -9.34) * mm, "end": v(0.7, -9.26) * mm});
            skLineSegment(sketch, "E815", {"start": v(0.7, -9.26) * mm, "end": v(0.67, -9.18) * mm});
            skLineSegment(sketch, "E816", {"start": v(0.67, -9.18) * mm, "end": v(0.62, -9.1) * mm});
            skLineSegment(sketch, "E817", {"start": v(0.62, -9.1) * mm, "end": v(0.58, -9.01) * mm});
            skLineSegment(sketch, "E818", {"start": v(0.58, -9.01) * mm, "end": v(0.53, -8.93) * mm});
            skLineSegment(sketch, "E819", {"start": v(0.53, -8.93) * mm, "end": v(0.47, -8.85) * mm});
            skLineSegment(sketch, "E820", {"start": v(0.47, -8.85) * mm, "end": v(0.42, -8.77) * mm});
            skLineSegment(sketch, "E821", {"start": v(0.42, -8.77) * mm, "end": v(0.35, -8.7) * mm});
            skLineSegment(sketch, "E822", {"start": v(0.35, -8.7) * mm, "end": v(0.22, -8.53) * mm});
            skLineSegment(sketch, "E823", {"start": v(0.22, -8.53) * mm, "end": v(0.08, -8.39) * mm});
            skLineSegment(sketch, "E824", {"start": v(0.08, -8.39) * mm, "end": v(-0.05, -8.26) * mm});
            skLineSegment(sketch, "E825", {"start": v(-0.05, -8.26) * mm, "end": v(-0.11, -8.2) * mm});
            skLineSegment(sketch, "E826", {"start": v(-0.11, -8.2) * mm, "end": v(-0.18, -8.15) * mm});
            skLineSegment(sketch, "E827", {"start": v(-0.18, -8.15) * mm, "end": v(-0.24, -8.1) * mm});
            skLineSegment(sketch, "E828", {"start": v(-0.24, -8.1) * mm, "end": v(-0.3, -8.06) * mm});
            skLineSegment(sketch, "E829", {"start": v(-0.3, -8.06) * mm, "end": v(-0.36, -8.02) * mm});
            skLineSegment(sketch, "E830", {"start": v(-0.36, -8.02) * mm, "end": v(-0.42, -7.98) * mm});
            skLineSegment(sketch, "E831", {"start": v(-0.42, -7.98) * mm, "end": v(-0.48, -7.95) * mm});
            skLineSegment(sketch, "E832", {"start": v(-0.48, -7.95) * mm, "end": v(-0.54, -7.93) * mm});
            skLineSegment(sketch, "E833", {"start": v(-0.54, -7.93) * mm, "end": v(-0.6, -7.9) * mm});
            skLineSegment(sketch, "E834", {"start": v(-0.6, -7.9) * mm, "end": v(-0.66, -7.89) * mm});
            skLineSegment(sketch, "E835", {"start": v(-0.66, -7.89) * mm, "end": v(-0.72, -7.88) * mm});
            skLineSegment(sketch, "E836", {"start": v(-0.72, -7.88) * mm, "end": v(-0.78, -7.87) * mm});
            skLineSegment(sketch, "E837", {"start": v(-0.78, -7.87) * mm, "end": v(-0.85, -7.86) * mm});
            skLineSegment(sketch, "E838", {"start": v(-0.85, -7.86) * mm, "end": v(-0.9, -7.86) * mm});
            skLineSegment(sketch, "E839", {"start": v(-0.9, -7.86) * mm, "end": v(-0.97, -7.87) * mm});
            skLineSegment(sketch, "E840", {"start": v(-0.97, -7.87) * mm, "end": v(-1.03, -7.87) * mm});
            skLineSegment(sketch, "E841", {"start": v(-1.03, -7.87) * mm, "end": v(-1.1, -7.89) * mm});
            skLineSegment(sketch, "E842", {"start": v(-1.1, -7.89) * mm, "end": v(-1.16, -7.9) * mm});
            skLineSegment(sketch, "E843", {"start": v(-1.16, -7.9) * mm, "end": v(-1.22, -7.92) * mm});
            skLineSegment(sketch, "E844", {"start": v(-1.22, -7.92) * mm, "end": v(-1.29, -7.95) * mm});
            skLineSegment(sketch, "E845", {"start": v(-1.29, -7.95) * mm, "end": v(-1.35, -7.98) * mm});
            skLineSegment(sketch, "E846", {"start": v(-1.35, -7.98) * mm, "end": v(-1.42, -8) * mm});
            skLineSegment(sketch, "E847", {"start": v(-1.42, -8) * mm, "end": v(-1.49, -8.05) * mm});
            skLineSegment(sketch, "E848", {"start": v(-1.49, -8.05) * mm, "end": v(-1.56, -8.09) * mm});
            skLineSegment(sketch, "E849", {"start": v(-1.56, -8.09) * mm, "end": v(-1.7, -8.18) * mm});
            skLineSegment(sketch, "E850", {"start": v(-1.7, -8.18) * mm, "end": v(-1.81, -8.25) * mm});
            skLineSegment(sketch, "E851", {"start": v(-1.81, -8.25) * mm, "end": v(-1.92, -8.32) * mm});
            skLineSegment(sketch, "E852", {"start": v(-1.92, -8.32) * mm, "end": v(-2.03, -8.38) * mm});
            skLineSegment(sketch, "E853", {"start": v(-2.03, -8.38) * mm, "end": v(-2.13, -8.43) * mm});
            skLineSegment(sketch, "E854", {"start": v(-2.13, -8.43) * mm, "end": v(-2.22, -8.47) * mm});
            skLineSegment(sketch, "E855", {"start": v(-2.22, -8.47) * mm, "end": v(-2.32, -8.51) * mm});
            skLineSegment(sketch, "E856", {"start": v(-2.32, -8.51) * mm, "end": v(-2.4, -8.54) * mm});
            skLineSegment(sketch, "E857", {"start": v(-2.4, -8.54) * mm, "end": v(-2.49, -8.57) * mm});
            skLineSegment(sketch, "E858", {"start": v(-2.49, -8.57) * mm, "end": v(-2.57, -8.59) * mm});
            skLineSegment(sketch, "E859", {"start": v(-2.57, -8.59) * mm, "end": v(-2.64, -8.6) * mm});
            skLineSegment(sketch, "E860", {"start": v(-2.64, -8.6) * mm, "end": v(-2.71, -8.6) * mm});
            skLineSegment(sketch, "E861", {"start": v(-2.71, -8.6) * mm, "end": v(-2.77, -8.6) * mm});
            skLineSegment(sketch, "E862", {"start": v(-2.77, -8.6) * mm, "end": v(-2.83, -8.6) * mm});
            skLineSegment(sketch, "E863", {"start": v(-2.83, -8.6) * mm, "end": v(-2.88, -8.59) * mm});
            skLineSegment(sketch, "E864", {"start": v(-2.88, -8.59) * mm, "end": v(-2.93, -8.57) * mm});
            skLineSegment(sketch, "E865", {"start": v(-2.93, -8.57) * mm, "end": v(-2.96, -8.55) * mm});
            skLineSegment(sketch, "E866", {"start": v(-2.96, -8.55) * mm, "end": v(-3, -8.52) * mm});
            skLineSegment(sketch, "E867", {"start": v(-3, -8.52) * mm, "end": v(-3.02, -8.5) * mm});
            skLineSegment(sketch, "E868", {"start": v(-3.02, -8.5) * mm, "end": v(-3.04, -8.46) * mm});
            skLineSegment(sketch, "E869", {"start": v(-3.04, -8.46) * mm, "end": v(-3.05, -8.41) * mm});
            skLineSegment(sketch, "E870", {"start": v(-3.05, -8.41) * mm, "end": v(-3.05, -8.37) * mm});
            skLineSegment(sketch, "E871", {"start": v(-3.05, -8.37) * mm, "end": v(-3.04, -8.32) * mm});
            skLineSegment(sketch, "E872", {"start": v(-3.04, -8.32) * mm, "end": v(-3.03, -8.27) * mm});
            skLineSegment(sketch, "E873", {"start": v(-3.03, -8.27) * mm, "end": v(-3, -8.21) * mm});
            skLineSegment(sketch, "E874", {"start": v(-3, -8.21) * mm, "end": v(-2.97, -8.15) * mm});
            skLineSegment(sketch, "E875", {"start": v(-2.97, -8.15) * mm, "end": v(-2.93, -8.09) * mm});
            skLineSegment(sketch, "E876", {"start": v(-2.93, -8.09) * mm, "end": v(-2.88, -8.02) * mm});
            skLineSegment(sketch, "E877", {"start": v(-2.88, -8.02) * mm, "end": v(-2.82, -7.95) * mm});
            skLineSegment(sketch, "E878", {"start": v(-2.82, -7.95) * mm, "end": v(-2.75, -7.88) * mm});
            skLineSegment(sketch, "E879", {"start": v(-2.75, -7.88) * mm, "end": v(-2.67, -7.8) * mm});
            skLineSegment(sketch, "E880", {"start": v(-2.67, -7.8) * mm, "end": v(-2.58, -7.72) * mm});
            skLineSegment(sketch, "E881", {"start": v(-2.58, -7.72) * mm, "end": v(-2.48, -7.64) * mm});
            skLineSegment(sketch, "E882", {"start": v(-2.48, -7.64) * mm, "end": v(-2.3, -7.5) * mm});
            skLineSegment(sketch, "E883", {"start": v(-2.3, -7.5) * mm, "end": v(-2.22, -7.43) * mm});
            skLineSegment(sketch, "E884", {"start": v(-2.22, -7.43) * mm, "end": v(-2.16, -7.37) * mm});
            skLineSegment(sketch, "E885", {"start": v(-2.16, -7.37) * mm, "end": v(-2.11, -7.32) * mm});
            skLineSegment(sketch, "E886", {"start": v(-2.11, -7.32) * mm, "end": v(-2.08, -7.27) * mm});
            skLineSegment(sketch, "E887", {"start": v(-2.08, -7.27) * mm, "end": v(-2.06, -7.24) * mm});
            skLineSegment(sketch, "E888", {"start": v(-2.06, -7.24) * mm, "end": v(-2.06, -7.21) * mm});
            skLineSegment(sketch, "E889", {"start": v(-2.06, -7.21) * mm, "end": v(-2.05, -7.19) * mm});
            skLineSegment(sketch, "E890", {"start": v(-2.05, -7.19) * mm, "end": v(-2.05, -7.16) * mm});
            skLineSegment(sketch, "E891", {"start": v(-2.05, -7.16) * mm, "end": v(-2.05, -7.13) * mm});
            skLineSegment(sketch, "E892", {"start": v(-2.05, -7.13) * mm, "end": v(-2.05, -7.1) * mm});
            skLineSegment(sketch, "E893", {"start": v(-2.05, -7.1) * mm, "end": v(-2.07, -7.03) * mm});
            skLineSegment(sketch, "E894", {"start": v(-2.07, -7.03) * mm, "end": v(-2.1, -6.96) * mm});
            skLineSegment(sketch, "E895", {"start": v(-2.1, -6.96) * mm, "end": v(-2.15, -6.88) * mm});
            skLineSegment(sketch, "E896", {"start": v(-2.15, -6.88) * mm, "end": v(-2.2, -6.79) * mm});
            skLineSegment(sketch, "E897", {"start": v(-2.2, -6.79) * mm, "end": v(-2.28, -6.69) * mm});
            skLineSegment(sketch, "E898", {"start": v(-2.28, -6.69) * mm, "end": v(-2.46, -6.43) * mm});
            skLineSegment(sketch, "E899", {"start": v(-2.46, -6.43) * mm, "end": v(-2.53, -6.33) * mm});
            skLineSegment(sketch, "E900", {"start": v(-2.53, -6.33) * mm, "end": v(-2.6, -6.22) * mm});
            skLineSegment(sketch, "E901", {"start": v(-2.6, -6.22) * mm, "end": v(-2.66, -6.1) * mm});
            skLineSegment(sketch, "E902", {"start": v(-2.66, -6.1) * mm, "end": v(-2.71, -6) * mm});
            skLineSegment(sketch, "E903", {"start": v(-2.71, -6) * mm, "end": v(-2.77, -5.88) * mm});
            skLineSegment(sketch, "E904", {"start": v(-2.77, -5.88) * mm, "end": v(-2.81, -5.76) * mm});
            skLineSegment(sketch, "E905", {"start": v(-2.81, -5.76) * mm, "end": v(-2.86, -5.64) * mm});
            skLineSegment(sketch, "E906", {"start": v(-2.86, -5.64) * mm, "end": v(-2.9, -5.52) * mm});
            skLineSegment(sketch, "E907", {"start": v(-2.9, -5.52) * mm, "end": v(-2.93, -5.4) * mm});
            skLineSegment(sketch, "E908", {"start": v(-2.93, -5.4) * mm, "end": v(-2.96, -5.27) * mm});
            skLineSegment(sketch, "E909", {"start": v(-2.96, -5.27) * mm, "end": v(-2.98, -5.14) * mm});
            skLineSegment(sketch, "E910", {"start": v(-2.98, -5.14) * mm, "end": v(-3, -5.01) * mm});
            skLineSegment(sketch, "E911", {"start": v(-3, -5.01) * mm, "end": v(-3.01, -4.89) * mm});
            skLineSegment(sketch, "E912", {"start": v(-3.01, -4.89) * mm, "end": v(-3.02, -4.76) * mm});
            skLineSegment(sketch, "E913", {"start": v(-3.02, -4.76) * mm, "end": v(-3.03, -4.63) * mm});
            skLineSegment(sketch, "E914", {"start": v(-3.03, -4.63) * mm, "end": v(-3.03, -4.5) * mm});
            skLineSegment(sketch, "E915", {"start": v(-3.03, -4.5) * mm, "end": v(-3.02, -4.37) * mm});
            skLineSegment(sketch, "E916", {"start": v(-3.02, -4.37) * mm, "end": v(-3.01, -4.25) * mm});
            skLineSegment(sketch, "E917", {"start": v(-3.01, -4.25) * mm, "end": v(-3, -4.12) * mm});
            skLineSegment(sketch, "E918", {"start": v(-3, -4.12) * mm, "end": v(-2.98, -4) * mm});
            skLineSegment(sketch, "E919", {"start": v(-2.98, -4) * mm, "end": v(-2.95, -3.87) * mm});
            skLineSegment(sketch, "E920", {"start": v(-2.95, -3.87) * mm, "end": v(-2.93, -3.75) * mm});
            skLineSegment(sketch, "E921", {"start": v(-2.93, -3.75) * mm, "end": v(-2.9, -3.63) * mm});
            skLineSegment(sketch, "E922", {"start": v(-2.9, -3.63) * mm, "end": v(-2.86, -3.51) * mm});
            skLineSegment(sketch, "E923", {"start": v(-2.86, -3.51) * mm, "end": v(-2.81, -3.4) * mm});
            skLineSegment(sketch, "E924", {"start": v(-2.81, -3.4) * mm, "end": v(-2.77, -3.28) * mm});
            skLineSegment(sketch, "E925", {"start": v(-2.77, -3.28) * mm, "end": v(-2.71, -3.17) * mm});
            skLineSegment(sketch, "E926", {"start": v(-2.71, -3.17) * mm, "end": v(-2.66, -3.07) * mm});
            skLineSegment(sketch, "E927", {"start": v(-2.66, -3.07) * mm, "end": v(-2.6, -2.97) * mm});
            skLineSegment(sketch, "E928", {"start": v(-2.6, -2.97) * mm, "end": v(-2.53, -2.87) * mm});
            skLineSegment(sketch, "E929", {"start": v(-2.53, -2.87) * mm, "end": v(-2.46, -2.77) * mm});
            skLineSegment(sketch, "E930", {"start": v(-2.46, -2.77) * mm, "end": v(-2.39, -2.68) * mm});
            skLineSegment(sketch, "E931", {"start": v(-2.39, -2.68) * mm, "end": v(-2.25, -2.53) * mm});
            skLineSegment(sketch, "E932", {"start": v(-2.25, -2.53) * mm, "end": v(-2.1, -2.39) * mm});
            skLineSegment(sketch, "E933", {"start": v(-2.1, -2.39) * mm, "end": v(-1.96, -2.25) * mm});
            skLineSegment(sketch, "E934", {"start": v(-1.96, -2.25) * mm, "end": v(-1.81, -2.13) * mm});
            skLineSegment(sketch, "E935", {"start": v(-1.81, -2.13) * mm, "end": v(-1.66, -2) * mm});
            skLineSegment(sketch, "E936", {"start": v(-1.66, -2) * mm, "end": v(-1.5, -1.9) * mm});
            skLineSegment(sketch, "E937", {"start": v(-1.5, -1.9) * mm, "end": v(-1.35, -1.8) * mm});
            skLineSegment(sketch, "E938", {"start": v(-1.35, -1.8) * mm, "end": v(-1.2, -1.72) * mm});
            skLineSegment(sketch, "E939", {"start": v(-1.2, -1.72) * mm, "end": v(-1.03, -1.64) * mm});
            skLineSegment(sketch, "E940", {"start": v(-1.03, -1.64) * mm, "end": v(-0.87, -1.57) * mm});
            skLineSegment(sketch, "E941", {"start": v(-0.87, -1.57) * mm, "end": v(-0.85, -1.56) * mm});
            skLineSegment(sketch, "E942", {"start": v(-0.85, -1.56) * mm, "end": v(-0.94, -1.53) * mm});
            skLineSegment(sketch, "E943", {"start": v(-0.94, -1.53) * mm, "end": v(-1.06, -1.48) * mm});
            skLineSegment(sketch, "E944", {"start": v(-1.06, -1.48) * mm, "end": v(-1.26, -1.38) * mm});
            skLineSegment(sketch, "E945", {"start": v(-1.26, -1.38) * mm, "end": v(-1.4, -1.32) * mm});
            skLineSegment(sketch, "E946", {"start": v(-1.4, -1.32) * mm, "end": v(-1.47, -1.29) * mm});
            skLineSegment(sketch, "E947", {"start": v(-1.47, -1.29) * mm, "end": v(-1.54, -1.24) * mm});
            skLineSegment(sketch, "E948", {"start": v(-1.54, -1.24) * mm, "end": v(-1.6, -1.19) * mm});
            skLineSegment(sketch, "E949", {"start": v(-1.6, -1.19) * mm, "end": v(-1.67, -1.13) * mm});
            skLineSegment(sketch, "E950", {"start": v(-1.67, -1.13) * mm, "end": v(-1.74, -1.07) * mm});
            skLineSegment(sketch, "E951", {"start": v(-1.74, -1.07) * mm, "end": v(-1.8, -1) * mm});
            skLineSegment(sketch, "E952", {"start": v(-1.8, -1) * mm, "end": v(-1.85, -0.94) * mm});
            skLineSegment(sketch, "E953", {"start": v(-1.85, -0.94) * mm, "end": v(-1.9, -0.87) * mm});
            skLineSegment(sketch, "E954", {"start": v(-1.9, -0.87) * mm, "end": v(-1.95, -0.8) * mm});
            skLineSegment(sketch, "E955", {"start": v(-1.95, -0.8) * mm, "end": v(-1.99, -0.72) * mm});
            skLineSegment(sketch, "E956", {"start": v(-1.99, -0.72) * mm, "end": v(-2.02, -0.64) * mm});
            skLineSegment(sketch, "E957", {"start": v(-2.02, -0.64) * mm, "end": v(-2.06, -0.56) * mm});
            skLineSegment(sketch, "E958", {"start": v(-2.06, -0.56) * mm, "end": v(-2.08, -0.47) * mm});
            skLineSegment(sketch, "E959", {"start": v(-2.08, -0.47) * mm, "end": v(-2.1, -0.39) * mm});
            skLineSegment(sketch, "E960", {"start": v(-2.1, -0.39) * mm, "end": v(-2.12, -0.3) * mm});
            skLineSegment(sketch, "E961", {"start": v(-2.12, -0.3) * mm, "end": v(-2.13, -0.2) * mm});
            skLineSegment(sketch, "E962", {"start": v(-2.13, -0.2) * mm, "end": v(-2.13, -0.12) * mm});
            skLineSegment(sketch, "E963", {"start": v(-2.13, -0.12) * mm, "end": v(-2.13, -0.05) * mm});
            skLineSegment(sketch, "E964", {"start": v(-2.13, -0.05) * mm, "end": v(-2.12, 0.02) * mm});
            skLineSegment(sketch, "E965", {"start": v(-2.12, 0.02) * mm, "end": v(-2.11, 0.1) * mm});
            skLineSegment(sketch, "E966", {"start": v(-2.11, 0.1) * mm, "end": v(-2.1, 0.16) * mm});
            skLineSegment(sketch, "E967", {"start": v(-2.1, 0.16) * mm, "end": v(-2.09, 0.22) * mm});
            skLineSegment(sketch, "E968", {"start": v(-2.09, 0.22) * mm, "end": v(-2.07, 0.29) * mm});
            skLineSegment(sketch, "E969", {"start": v(-2.07, 0.29) * mm, "end": v(-2.05, 0.35) * mm});
            skLineSegment(sketch, "E970", {"start": v(-2.05, 0.35) * mm, "end": v(-2.02, 0.41) * mm});
            skLineSegment(sketch, "E971", {"start": v(-2.02, 0.41) * mm, "end": v(-2, 0.48) * mm});
            skLineSegment(sketch, "E972", {"start": v(-2, 0.48) * mm, "end": v(-1.96, 0.53) * mm});
            skLineSegment(sketch, "E973", {"start": v(-1.96, 0.53) * mm, "end": v(-1.93, 0.6) * mm});
            skLineSegment(sketch, "E974", {"start": v(-1.93, 0.6) * mm, "end": v(-1.9, 0.65) * mm});
            skLineSegment(sketch, "E975", {"start": v(-1.9, 0.65) * mm, "end": v(-1.86, 0.7) * mm});
            skLineSegment(sketch, "E976", {"start": v(-1.86, 0.7) * mm, "end": v(-1.82, 0.75) * mm});
            skLineSegment(sketch, "E977", {"start": v(-1.82, 0.75) * mm, "end": v(-1.77, 0.8) * mm});
            skLineSegment(sketch, "E978", {"start": v(-1.77, 0.8) * mm, "end": v(-1.73, 0.85) * mm});
            skLineSegment(sketch, "E979", {"start": v(-1.73, 0.85) * mm, "end": v(-1.68, 0.9) * mm});
            skLineSegment(sketch, "E980", {"start": v(-1.68, 0.9) * mm, "end": v(-1.63, 0.94) * mm});
            skLineSegment(sketch, "E981", {"start": v(-1.63, 0.94) * mm, "end": v(-1.58, 0.98) * mm});
            skLineSegment(sketch, "E982", {"start": v(-1.58, 0.98) * mm, "end": v(-1.53, 1.01) * mm});
            skLineSegment(sketch, "E983", {"start": v(-1.53, 1.01) * mm, "end": v(-1.47, 1.05) * mm});
            skLineSegment(sketch, "E984", {"start": v(-1.47, 1.05) * mm, "end": v(-1.42, 1.08) * mm});
            skLineSegment(sketch, "E985", {"start": v(-1.42, 1.08) * mm, "end": v(-1.36, 1.11) * mm});
            skLineSegment(sketch, "E986", {"start": v(-1.36, 1.11) * mm, "end": v(-1.3, 1.14) * mm});
            skLineSegment(sketch, "E987", {"start": v(-1.3, 1.14) * mm, "end": v(-1.23, 1.16) * mm});
            skLineSegment(sketch, "E988", {"start": v(-1.23, 1.16) * mm, "end": v(-1.17, 1.19) * mm});
            skLineSegment(sketch, "E989", {"start": v(-1.17, 1.19) * mm, "end": v(-1.1, 1.2) * mm});
            skLineSegment(sketch, "E990", {"start": v(-1.1, 1.2) * mm, "end": v(-1.04, 1.22) * mm});
            skLineSegment(sketch, "E991", {"start": v(-1.04, 1.22) * mm, "end": v(-0.97, 1.23) * mm});
            skLineSegment(sketch, "E992", {"start": v(-0.97, 1.23) * mm, "end": v(-0.9, 1.24) * mm});
            skLineSegment(sketch, "E993", {"start": v(-0.9, 1.24) * mm, "end": v(-0.84, 1.25) * mm});
            skLineSegment(sketch, "E994", {"start": v(-0.84, 1.25) * mm, "end": v(-0.76, 1.25) * mm});
            skLineSegment(sketch, "E995", {"start": v(-0.76, 1.25) * mm, "end": v(-0.7, 1.25) * mm});
            skLineSegment(sketch, "E996", {"start": v(-0.7, 1.25) * mm, "end": v(-0.63, 1.24) * mm});
            skLineSegment(sketch, "E997", {"start": v(-0.63, 1.24) * mm, "end": v(-0.56, 1.23) * mm});
            skLineSegment(sketch, "E998", {"start": v(-0.56, 1.23) * mm, "end": v(-0.5, 1.22) * mm});
            skLineSegment(sketch, "E999", {"start": v(-0.5, 1.22) * mm, "end": v(-0.42, 1.2) * mm});
            skLineSegment(sketch, "E1000", {"start": v(-0.42, 1.2) * mm, "end": v(-0.36, 1.19) * mm});
            skLineSegment(sketch, "E1001", {"start": v(-0.36, 1.19) * mm, "end": v(-0.3, 1.16) * mm});
            skLineSegment(sketch, "E1002", {"start": v(-0.3, 1.16) * mm, "end": v(-0.23, 1.14) * mm});
            skLineSegment(sketch, "E1003", {"start": v(-0.23, 1.14) * mm, "end": v(-0.17, 1.11) * mm});
            skLineSegment(sketch, "E1004", {"start": v(-0.17, 1.11) * mm, "end": v(-0.11, 1.08) * mm});
            skLineSegment(sketch, "E1005", {"start": v(-0.11, 1.08) * mm, "end": v(-0.06, 1.05) * mm});
            skLineSegment(sketch, "E1006", {"start": v(-0.06, 1.05) * mm, "end": v(0, 1.01) * mm});
            skLineSegment(sketch, "E1007", {"start": v(0, 1.01) * mm, "end": v(0.05, 0.98) * mm});
            skLineSegment(sketch, "E1008", {"start": v(0.05, 0.98) * mm, "end": v(0.1, 0.94) * mm});
            skLineSegment(sketch, "E1009", {"start": v(0.1, 0.94) * mm, "end": v(0.15, 0.9) * mm});
            skLineSegment(sketch, "E1010", {"start": v(0.15, 0.9) * mm, "end": v(0.2, 0.85) * mm});
            skLineSegment(sketch, "E1011", {"start": v(0.2, 0.85) * mm, "end": v(0.24, 0.8) * mm});
            skLineSegment(sketch, "E1012", {"start": v(0.24, 0.8) * mm, "end": v(0.29, 0.75) * mm});
            skLineSegment(sketch, "E1013", {"start": v(0.29, 0.75) * mm, "end": v(0.33, 0.7) * mm});
            skLineSegment(sketch, "E1014", {"start": v(0.33, 0.7) * mm, "end": v(0.37, 0.65) * mm});
            skLineSegment(sketch, "E1015", {"start": v(0.37, 0.65) * mm, "end": v(0.4, 0.6) * mm});
            skLineSegment(sketch, "E1016", {"start": v(0.4, 0.6) * mm, "end": v(0.43, 0.53) * mm});
            skLineSegment(sketch, "E1017", {"start": v(0.43, 0.53) * mm, "end": v(0.46, 0.48) * mm});
            skLineSegment(sketch, "E1018", {"start": v(0.46, 0.48) * mm, "end": v(0.5, 0.41) * mm});
            skLineSegment(sketch, "E1019", {"start": v(0.5, 0.41) * mm, "end": v(0.52, 0.35) * mm});
            skLineSegment(sketch, "E1020", {"start": v(0.52, 0.35) * mm, "end": v(0.54, 0.29) * mm});
            skLineSegment(sketch, "E1021", {"start": v(0.54, 0.29) * mm, "end": v(0.56, 0.22) * mm});
            skLineSegment(sketch, "E1022", {"start": v(0.56, 0.22) * mm, "end": v(0.57, 0.16) * mm});
            skLineSegment(sketch, "E1023", {"start": v(0.57, 0.16) * mm, "end": v(0.58, 0.1) * mm});
            skLineSegment(sketch, "E1024", {"start": v(0.58, 0.1) * mm, "end": v(0.6, 0.02) * mm});
            skLineSegment(sketch, "E1025", {"start": v(0.6, 0.02) * mm, "end": v(0.6, -0.05) * mm});
            skLineSegment(sketch, "E1026", {"start": v(0.6, -0.05) * mm, "end": v(0.6, -0.12) * mm});
            skLineSegment(sketch, "E1027", {"start": v(0.6, -0.12) * mm, "end": v(0.6, -0.18) * mm});
            skLineSegment(sketch, "E1028", {"start": v(0.6, -0.18) * mm, "end": v(0.6, -0.25) * mm});
            skLineSegment(sketch, "E1029", {"start": v(0.6, -0.25) * mm, "end": v(0.58, -0.31) * mm});
            skLineSegment(sketch, "E1030", {"start": v(0.58, -0.31) * mm, "end": v(0.57, -0.38) * mm});
            skLineSegment(sketch, "E1031", {"start": v(0.57, -0.38) * mm, "end": v(0.65, -0.38) * mm});
            skLineSegment(sketch, "E1032", {"start": v(0.65, -0.38) * mm, "end": v(0.73, -0.37) * mm});
            skLineSegment(sketch, "E1033", {"start": v(0.73, -0.37) * mm, "end": v(0.82, -0.35) * mm});
            skLineSegment(sketch, "E1034", {"start": v(0.82, -0.35) * mm, "end": v(0.92, -0.33) * mm});
            skLineSegment(sketch, "E1035", {"start": v(0.92, -0.33) * mm, "end": v(1.05, -0.3) * mm});
            skLineSegment(sketch, "E1036", {"start": v(1.05, -0.3) * mm, "end": v(1.17, -0.26) * mm});
            skLineSegment(sketch, "E1037", {"start": v(1.17, -0.26) * mm, "end": v(1.29, -0.2) * mm});
            skLineSegment(sketch, "E1038", {"start": v(1.29, -0.2) * mm, "end": v(1.4, -0.15) * mm});
            skLineSegment(sketch, "E1039", {"start": v(1.4, -0.15) * mm, "end": v(1.5, -0.09) * mm});
            skLineSegment(sketch, "E1040", {"start": v(1.5, -0.09) * mm, "end": v(1.6, -0.02) * mm});
            skLineSegment(sketch, "E1041", {"start": v(1.6, -0.02) * mm, "end": v(1.7, 0.06) * mm});
            skLineSegment(sketch, "E1042", {"start": v(1.7, 0.06) * mm, "end": v(1.79, 0.14) * mm});
            skLineSegment(sketch, "E1043", {"start": v(1.79, 0.14) * mm, "end": v(1.87, 0.22) * mm});
            skLineSegment(sketch, "E1044", {"start": v(1.87, 0.22) * mm, "end": v(1.95, 0.32) * mm});
            skLineSegment(sketch, "E1045", {"start": v(1.95, 0.32) * mm, "end": v(2.02, 0.41) * mm});
            skLineSegment(sketch, "E1046", {"start": v(2.02, 0.41) * mm, "end": v(2.08, 0.51) * mm});
            skLineSegment(sketch, "E1047", {"start": v(2.08, 0.51) * mm, "end": v(2.14, 0.62) * mm});
            skLineSegment(sketch, "E1048", {"start": v(2.14, 0.62) * mm, "end": v(2.19, 0.72) * mm});
            skLineSegment(sketch, "E1049", {"start": v(2.19, 0.72) * mm, "end": v(2.23, 0.83) * mm});
            skLineSegment(sketch, "E1050", {"start": v(2.23, 0.83) * mm, "end": v(2.26, 0.95) * mm});
            skLineSegment(sketch, "E1051", {"start": v(2.26, 0.95) * mm, "end": v(2.3, 1.06) * mm});
            skLineSegment(sketch, "E1052", {"start": v(2.3, 1.06) * mm, "end": v(2.32, 1.18) * mm});
            skLineSegment(sketch, "E1053", {"start": v(2.32, 1.18) * mm, "end": v(2.33, 1.3) * mm});
            skLineSegment(sketch, "E1054", {"start": v(2.33, 1.3) * mm, "end": v(2.34, 1.41) * mm});
            skLineSegment(sketch, "E1055", {"start": v(2.34, 1.41) * mm, "end": v(2.34, 1.53) * mm});
            skLineSegment(sketch, "E1056", {"start": v(2.34, 1.53) * mm, "end": v(2.33, 1.65) * mm});
            skLineSegment(sketch, "E1057", {"start": v(2.33, 1.65) * mm, "end": v(2.31, 1.77) * mm});
            skLineSegment(sketch, "E1058", {"start": v(2.31, 1.77) * mm, "end": v(2.3, 1.9) * mm});
            skLineSegment(sketch, "E1059", {"start": v(2.3, 1.9) * mm, "end": v(2.26, 2) * mm});
            skLineSegment(sketch, "E1060", {"start": v(2.26, 2) * mm, "end": v(2.22, 2.12) * mm});
            skLineSegment(sketch, "E1061", {"start": v(2.22, 2.12) * mm, "end": v(2.17, 2.24) * mm});
            skLineSegment(sketch, "E1062", {"start": v(2.17, 2.24) * mm, "end": v(2.12, 2.35) * mm});
            skLineSegment(sketch, "E1063", {"start": v(2.12, 2.35) * mm, "end": v(2.05, 2.46) * mm});
            skLineSegment(sketch, "E1064", {"start": v(2.05, 2.46) * mm, "end": v(1.98, 2.57) * mm});
            skLineSegment(sketch, "E1065", {"start": v(1.98, 2.57) * mm, "end": v(1.9, 2.67) * mm});
            skLineSegment(sketch, "E1066", {"start": v(1.9, 2.67) * mm, "end": v(1.8, 2.77) * mm});
            skLineSegment(sketch, "E1067", {"start": v(1.8, 2.77) * mm, "end": v(1.75, 2.83) * mm});
            skLineSegment(sketch, "E1068", {"start": v(1.75, 2.83) * mm, "end": v(1.68, 2.89) * mm});
            skLineSegment(sketch, "E1069", {"start": v(1.68, 2.89) * mm, "end": v(1.62, 2.94) * mm});
            skLineSegment(sketch, "E1070", {"start": v(1.62, 2.94) * mm, "end": v(1.55, 3) * mm});
            skLineSegment(sketch, "E1071", {"start": v(1.55, 3) * mm, "end": v(1.49, 3.04) * mm});
            skLineSegment(sketch, "E1072", {"start": v(1.49, 3.04) * mm, "end": v(1.42, 3.08) * mm});
            skLineSegment(sketch, "E1073", {"start": v(1.42, 3.08) * mm, "end": v(1.35, 3.12) * mm});
            skLineSegment(sketch, "E1074", {"start": v(1.35, 3.12) * mm, "end": v(1.28, 3.16) * mm});
            skLineSegment(sketch, "E1075", {"start": v(1.28, 3.16) * mm, "end": v(1.22, 3.2) * mm});
            skLineSegment(sketch, "E1076", {"start": v(1.22, 3.2) * mm, "end": v(1.15, 3.22) * mm});
            skLineSegment(sketch, "E1077", {"start": v(1.15, 3.22) * mm, "end": v(1.08, 3.25) * mm});
            skLineSegment(sketch, "E1078", {"start": v(1.08, 3.25) * mm, "end": v(1.01, 3.27) * mm});
            skLineSegment(sketch, "E1079", {"start": v(1.01, 3.27) * mm, "end": v(0.95, 3.3) * mm});
            skLineSegment(sketch, "E1080", {"start": v(0.95, 3.3) * mm, "end": v(0.88, 3.3) * mm});
            skLineSegment(sketch, "E1081", {"start": v(0.88, 3.3) * mm, "end": v(0.82, 3.32) * mm});
            skLineSegment(sketch, "E1082", {"start": v(0.82, 3.32) * mm, "end": v(0.76, 3.33) * mm});
            skLineSegment(sketch, "E1083", {"start": v(0.76, 3.33) * mm, "end": v(0.7, 3.33) * mm});
            skLineSegment(sketch, "E1084", {"start": v(0.7, 3.33) * mm, "end": v(0.64, 3.33) * mm});
            skLineSegment(sketch, "E1085", {"start": v(0.64, 3.33) * mm, "end": v(0.58, 3.33) * mm});
            skLineSegment(sketch, "E1086", {"start": v(0.58, 3.33) * mm, "end": v(0.53, 3.32) * mm});
            skLineSegment(sketch, "E1087", {"start": v(0.53, 3.32) * mm, "end": v(0.47, 3.31) * mm});
            skLineSegment(sketch, "E1088", {"start": v(0.47, 3.31) * mm, "end": v(0.43, 3.3) * mm});
            skLineSegment(sketch, "E1089", {"start": v(0.43, 3.3) * mm, "end": v(0.38, 3.28) * mm});
            skLineSegment(sketch, "E1090", {"start": v(0.38, 3.28) * mm, "end": v(0.34, 3.26) * mm});
            skLineSegment(sketch, "E1091", {"start": v(0.34, 3.26) * mm, "end": v(0.3, 3.23) * mm});
            skLineSegment(sketch, "E1092", {"start": v(0.3, 3.23) * mm, "end": v(0.27, 3.2) * mm});
            skLineSegment(sketch, "E1093", {"start": v(0.27, 3.2) * mm, "end": v(0.24, 3.17) * mm});
            skLineSegment(sketch, "E1094", {"start": v(0.24, 3.17) * mm, "end": v(0.2, 3.13) * mm});
            skLineSegment(sketch, "E1095", {"start": v(0.2, 3.13) * mm, "end": v(0.19, 3.09) * mm});
            skLineSegment(sketch, "E1096", {"start": v(0.19, 3.09) * mm, "end": v(0.17, 3.04) * mm});
            skLineSegment(sketch, "E1097", {"start": v(0.17, 3.04) * mm, "end": v(0.16, 3) * mm});
            skLineSegment(sketch, "E1098", {"start": v(0.16, 3) * mm, "end": v(0.15, 2.94) * mm});
            skLineSegment(sketch, "E1099", {"start": v(0.15, 2.94) * mm, "end": v(0.12, 2.85) * mm});
            skLineSegment(sketch, "E1100", {"start": v(0.12, 2.85) * mm, "end": v(0.09, 2.75) * mm});
            skLineSegment(sketch, "E1101", {"start": v(0.09, 2.75) * mm, "end": v(0.05, 2.66) * mm});
            skLineSegment(sketch, "E1102", {"start": v(0.05, 2.66) * mm, "end": v(0, 2.58) * mm});
            skLineSegment(sketch, "E1103", {"start": v(0, 2.58) * mm, "end": v(-0.06, 2.5) * mm});
            skLineSegment(sketch, "E1104", {"start": v(-0.06, 2.5) * mm, "end": v(-0.12, 2.42) * mm});
            skLineSegment(sketch, "E1105", {"start": v(-0.12, 2.42) * mm, "end": v(-0.18, 2.35) * mm});
            skLineSegment(sketch, "E1106", {"start": v(-0.18, 2.35) * mm, "end": v(-0.26, 2.3) * mm});
            skLineSegment(sketch, "E1107", {"start": v(-0.26, 2.3) * mm, "end": v(-0.33, 2.23) * mm});
            skLineSegment(sketch, "E1108", {"start": v(-0.33, 2.23) * mm, "end": v(-0.42, 2.18) * mm});
            skLineSegment(sketch, "E1109", {"start": v(-0.42, 2.18) * mm, "end": v(-0.5, 2.14) * mm});
            skLineSegment(sketch, "E1110", {"start": v(-0.5, 2.14) * mm, "end": v(-0.6, 2.1) * mm});
            skLineSegment(sketch, "E1111", {"start": v(-0.6, 2.1) * mm, "end": v(-0.69, 2.07) * mm});
            skLineSegment(sketch, "E1112", {"start": v(-0.69, 2.07) * mm, "end": v(-0.79, 2.05) * mm});
            skLineSegment(sketch, "E1113", {"start": v(-0.79, 2.05) * mm, "end": v(-0.88, 2.04) * mm});
            skLineSegment(sketch, "E1114", {"start": v(-0.88, 2.04) * mm, "end": v(-0.99, 2.03) * mm});
            skLineSegment(sketch, "E1115", {"start": v(-0.99, 2.03) * mm, "end": v(-1.05, 2.03) * mm});
            skLineSegment(sketch, "E1116", {"start": v(-1.05, 2.03) * mm, "end": v(-1.1, 2.04) * mm});
            skLineSegment(sketch, "E1117", {"start": v(-1.1, 2.04) * mm, "end": v(-1.16, 2.05) * mm});
            skLineSegment(sketch, "E1118", {"start": v(-1.16, 2.05) * mm, "end": v(-1.22, 2.06) * mm});
            skLineSegment(sketch, "E1119", {"start": v(-1.22, 2.06) * mm, "end": v(-1.28, 2.07) * mm});
            skLineSegment(sketch, "E1120", {"start": v(-1.28, 2.07) * mm, "end": v(-1.33, 2.09) * mm});
            skLineSegment(sketch, "E1121", {"start": v(-1.33, 2.09) * mm, "end": v(-1.39, 2.1) * mm});
            skLineSegment(sketch, "E1122", {"start": v(-1.39, 2.1) * mm, "end": v(-1.44, 2.12) * mm});
            skLineSegment(sketch, "E1123", {"start": v(-1.44, 2.12) * mm, "end": v(-1.54, 2.17) * mm});
            skLineSegment(sketch, "E1124", {"start": v(-1.54, 2.17) * mm, "end": v(-1.64, 2.23) * mm});
            skLineSegment(sketch, "E1125", {"start": v(-1.64, 2.23) * mm, "end": v(-1.73, 2.3) * mm});
            skLineSegment(sketch, "E1126", {"start": v(-1.73, 2.3) * mm, "end": v(-1.8, 2.37) * mm});
            skLineSegment(sketch, "E1127", {"start": v(-1.8, 2.37) * mm, "end": v(-1.89, 2.46) * mm});
            skLineSegment(sketch, "E1128", {"start": v(-1.89, 2.46) * mm, "end": v(-1.95, 2.55) * mm});
            skLineSegment(sketch, "E1129", {"start": v(-1.95, 2.55) * mm, "end": v(-2.01, 2.64) * mm});
            skLineSegment(sketch, "E1130", {"start": v(-2.01, 2.64) * mm, "end": v(-2.06, 2.74) * mm});
            skLineSegment(sketch, "E1131", {"start": v(-2.06, 2.74) * mm, "end": v(-2.08, 2.8) * mm});
            skLineSegment(sketch, "E1132", {"start": v(-2.08, 2.8) * mm, "end": v(-2.1, 2.85) * mm});
            skLineSegment(sketch, "E1133", {"start": v(-2.1, 2.85) * mm, "end": v(-2.11, 2.9) * mm});
            skLineSegment(sketch, "E1134", {"start": v(-2.11, 2.9) * mm, "end": v(-2.13, 2.96) * mm});
            skLineSegment(sketch, "E1135", {"start": v(-2.13, 2.96) * mm, "end": v(-2.14, 3.02) * mm});
            skLineSegment(sketch, "E1136", {"start": v(-2.14, 3.02) * mm, "end": v(-2.14, 3.08) * mm});
            skLineSegment(sketch, "E1137", {"start": v(-2.14, 3.08) * mm, "end": v(-2.15, 3.14) * mm});
            skLineSegment(sketch, "E1138", {"start": v(-2.15, 3.14) * mm, "end": v(-2.15, 3.2) * mm});
            skLineSegment(sketch, "E1139", {"start": v(-2.15, 3.2) * mm, "end": v(-2.15, 3.26) * mm});
            skLineSegment(sketch, "E1140", {"start": v(-2.15, 3.26) * mm, "end": v(-2.14, 3.32) * mm});
            skLineSegment(sketch, "E1141", {"start": v(-2.14, 3.32) * mm, "end": v(-2.14, 3.38) * mm});
            skLineSegment(sketch, "E1142", {"start": v(-2.14, 3.38) * mm, "end": v(-2.13, 3.43) * mm});
            skLineSegment(sketch, "E1143", {"start": v(-2.13, 3.43) * mm, "end": v(-2.11, 3.5) * mm});
            skLineSegment(sketch, "E1144", {"start": v(-2.11, 3.5) * mm, "end": v(-2.1, 3.55) * mm});
            skLineSegment(sketch, "E1145", {"start": v(-2.1, 3.55) * mm, "end": v(-2.08, 3.6) * mm});
            skLineSegment(sketch, "E1146", {"start": v(-2.08, 3.6) * mm, "end": v(-2.06, 3.65) * mm});
            skLineSegment(sketch, "E1147", {"start": v(-2.06, 3.65) * mm, "end": v(-2.03, 3.7) * mm});
            skLineSegment(sketch, "E1148", {"start": v(-2.03, 3.7) * mm, "end": v(-2, 3.76) * mm});
            skLineSegment(sketch, "E1149", {"start": v(-2, 3.76) * mm, "end": v(-1.95, 3.85) * mm});
            skLineSegment(sketch, "E1150", {"start": v(-1.95, 3.85) * mm, "end": v(-1.88, 3.94) * mm});
            skLineSegment(sketch, "E1151", {"start": v(-1.88, 3.94) * mm, "end": v(-1.8, 4.03) * mm});
            skLineSegment(sketch, "E1152", {"start": v(-1.8, 4.03) * mm, "end": v(-1.8, 4.04) * mm});
            skLineSegment(sketch, "E1153", {"start": v(-1.8, 4.04) * mm, "end": v(-1.69, 4.18) * mm});
            skLineSegment(sketch, "E1154", {"start": v(-1.69, 4.18) * mm, "end": v(-1.63, 4.26) * mm});
            skLineSegment(sketch, "E1155", {"start": v(-1.63, 4.26) * mm, "end": v(-1.57, 4.34) * mm});
            skLineSegment(sketch, "E1156", {"start": v(-1.57, 4.34) * mm, "end": v(-1.42, 4.52) * mm});
            skLineSegment(sketch, "E1157", {"start": v(-1.42, 4.52) * mm, "end": v(-1.37, 4.6) * mm});
            skLineSegment(sketch, "E1158", {"start": v(-1.37, 4.6) * mm, "end": v(-1.32, 4.67) * mm});
            skLineSegment(sketch, "E1159", {"start": v(-1.32, 4.67) * mm, "end": v(-1.28, 4.73) * mm});
            skLineSegment(sketch, "E1160", {"start": v(-1.28, 4.73) * mm, "end": v(-1.25, 4.8) * mm});
            skLineSegment(sketch, "E1161", {"start": v(-1.25, 4.8) * mm, "end": v(-1.23, 4.85) * mm});
            skLineSegment(sketch, "E1162", {"start": v(-1.23, 4.85) * mm, "end": v(-1.22, 4.9) * mm});
            skLineSegment(sketch, "E1163", {"start": v(-1.22, 4.9) * mm, "end": v(-1.22, 4.95) * mm});
            skLineSegment(sketch, "E1164", {"start": v(-1.22, 4.95) * mm, "end": v(-1.23, 5) * mm});
            skLineSegment(sketch, "E1165", {"start": v(-1.23, 5) * mm, "end": v(-1.25, 5.04) * mm});
            skLineSegment(sketch, "E1166", {"start": v(-1.25, 5.04) * mm, "end": v(-1.27, 5.1) * mm});
            skLineSegment(sketch, "E1167", {"start": v(-1.27, 5.1) * mm, "end": v(-1.3, 5.15) * mm});
            skLineSegment(sketch, "E1168", {"start": v(-1.3, 5.15) * mm, "end": v(-1.35, 5.2) * mm});
            skLineSegment(sketch, "E1169", {"start": v(-1.35, 5.2) * mm, "end": v(-1.46, 5.34) * mm});
            skLineSegment(sketch, "E1170", {"start": v(-1.46, 5.34) * mm, "end": v(-1.51, 5.4) * mm});
            skLineSegment(sketch, "E1171", {"start": v(-1.51, 5.4) * mm, "end": v(-1.56, 5.46) * mm});
            skLineSegment(sketch, "E1172", {"start": v(-1.56, 5.46) * mm, "end": v(-1.6, 5.53) * mm});
            skLineSegment(sketch, "E1173", {"start": v(-1.6, 5.53) * mm, "end": v(-1.65, 5.6) * mm});
            skLineSegment(sketch, "E1174", {"start": v(-1.65, 5.6) * mm, "end": v(-1.69, 5.68) * mm});
            skLineSegment(sketch, "E1175", {"start": v(-1.69, 5.68) * mm, "end": v(-1.72, 5.76) * mm});
            skLineSegment(sketch, "E1176", {"start": v(-1.72, 5.76) * mm, "end": v(-1.76, 5.85) * mm});
            skLineSegment(sketch, "E1177", {"start": v(-1.76, 5.85) * mm, "end": v(-1.79, 5.93) * mm});
            skLineSegment(sketch, "E1178", {"start": v(-1.79, 5.93) * mm, "end": v(-1.82, 6.02) * mm});
            skLineSegment(sketch, "E1179", {"start": v(-1.82, 6.02) * mm, "end": v(-1.84, 6.11) * mm});
            skLineSegment(sketch, "E1180", {"start": v(-1.84, 6.11) * mm, "end": v(-1.87, 6.2) * mm});
            skLineSegment(sketch, "E1181", {"start": v(-1.87, 6.2) * mm, "end": v(-1.89, 6.3) * mm});
            skLineSegment(sketch, "E1182", {"start": v(-1.89, 6.3) * mm, "end": v(-1.9, 6.4) * mm});
            skLineSegment(sketch, "E1183", {"start": v(-1.9, 6.4) * mm, "end": v(-1.92, 6.5) * mm});
            skLineSegment(sketch, "E1184", {"start": v(-1.92, 6.5) * mm, "end": v(-1.93, 6.6) * mm});
            skLineSegment(sketch, "E1185", {"start": v(-1.93, 6.6) * mm, "end": v(-1.94, 6.7) * mm});
            skLineSegment(sketch, "E1186", {"start": v(-1.94, 6.7) * mm, "end": v(-1.94, 6.8) * mm});
            skLineSegment(sketch, "E1187", {"start": v(-1.94, 6.8) * mm, "end": v(-1.95, 6.9) * mm});
            skLineSegment(sketch, "E1188", {"start": v(-1.95, 6.9) * mm, "end": v(-1.95, 7) * mm});
            skLineSegment(sketch, "E1189", {"start": v(-1.95, 7) * mm, "end": v(-1.94, 7.1) * mm});
            skLineSegment(sketch, "E1190", {"start": v(-1.94, 7.1) * mm, "end": v(-1.94, 7.2) * mm});
            skLineSegment(sketch, "E1191", {"start": v(-1.94, 7.2) * mm, "end": v(-1.93, 7.3) * mm});
            skLineSegment(sketch, "E1192", {"start": v(-1.93, 7.3) * mm, "end": v(-1.92, 7.4) * mm});
            skLineSegment(sketch, "E1193", {"start": v(-1.92, 7.4) * mm, "end": v(-1.9, 7.5) * mm});
            skLineSegment(sketch, "E1194", {"start": v(-1.9, 7.5) * mm, "end": v(-1.88, 7.6) * mm});
            skLineSegment(sketch, "E1195", {"start": v(-1.88, 7.6) * mm, "end": v(-1.86, 7.7) * mm});
            skLineSegment(sketch, "E1196", {"start": v(-1.86, 7.7) * mm, "end": v(-1.84, 7.8) * mm});
            skLineSegment(sketch, "E1197", {"start": v(-1.84, 7.8) * mm, "end": v(-1.81, 7.89) * mm});
            skLineSegment(sketch, "E1198", {"start": v(-1.81, 7.89) * mm, "end": v(-1.78, 7.98) * mm});
            skLineSegment(sketch, "E1199", {"start": v(-1.78, 7.98) * mm, "end": v(-1.75, 8.06) * mm});
            skLineSegment(sketch, "E1200", {"start": v(-1.75, 8.06) * mm, "end": v(-1.71, 8.15) * mm});
            skLineSegment(sketch, "E1201", {"start": v(-1.71, 8.15) * mm, "end": v(-1.67, 8.23) * mm});
            skLineSegment(sketch, "E1202", {"start": v(-1.67, 8.23) * mm, "end": v(-1.58, 8.4) * mm});
            skLineSegment(sketch, "E1203", {"start": v(-1.58, 8.4) * mm, "end": v(-1.51, 8.56) * mm});
            skLineSegment(sketch, "E1204", {"start": v(-1.51, 8.56) * mm, "end": v(-1.48, 8.62) * mm});
            skLineSegment(sketch, "E1205", {"start": v(-1.48, 8.62) * mm, "end": v(-1.46, 8.68) * mm});
            skLineSegment(sketch, "E1206", {"start": v(-1.46, 8.68) * mm, "end": v(-1.45, 8.74) * mm});
            skLineSegment(sketch, "E1207", {"start": v(-1.45, 8.74) * mm, "end": v(-1.44, 8.78) * mm});
            skLineSegment(sketch, "E1208", {"start": v(-1.44, 8.78) * mm, "end": v(-1.4, 9.1) * mm});
            skLineSegment(sketch, "E1209", {"start": v(-1.4, 9.1) * mm, "end": v(-1.35, 9.56) * mm});
            skLineSegment(sketch, "E1210", {"start": v(-1.35, 9.56) * mm, "end": v(-1.3, 10.1) * mm});
            skLineSegment(sketch, "E1211", {"start": v(-1.3, 10.1) * mm, "end": v(-1.24, 10.7) * mm});
            skLineSegment(sketch, "E1212", {"start": v(-1.24, 10.7) * mm, "end": v(-1.13, 12.06) * mm});
            skLineSegment(sketch, "E1213", {"start": v(-1.13, 12.06) * mm, "end": v(-1.01, 13.5) * mm});
            skLineSegment(sketch, "E1214", {"start": v(-1.01, 13.5) * mm, "end": v(-0.91, 14.92) * mm});
            skLineSegment(sketch, "E1215", {"start": v(-0.91, 14.92) * mm, "end": v(-0.08, 31.94) * mm});
            skCircle(sketch, "E1216", {"center": v(0.23, -18.03) * mm, "radius": 1 * mm});
            skCircle(sketch, "E1217", {"center": v(0.23, -18.03) * mm, "radius": 4 * mm});
            skSolve(sketch);
        }
        {
            var Q0;
            Q0=qSketchRegion(id+"F0",true);
            extrude(context, id + "F1", {"entities" : qUnion([Q0]), "depth" : 3 * mm});
        }
    });
